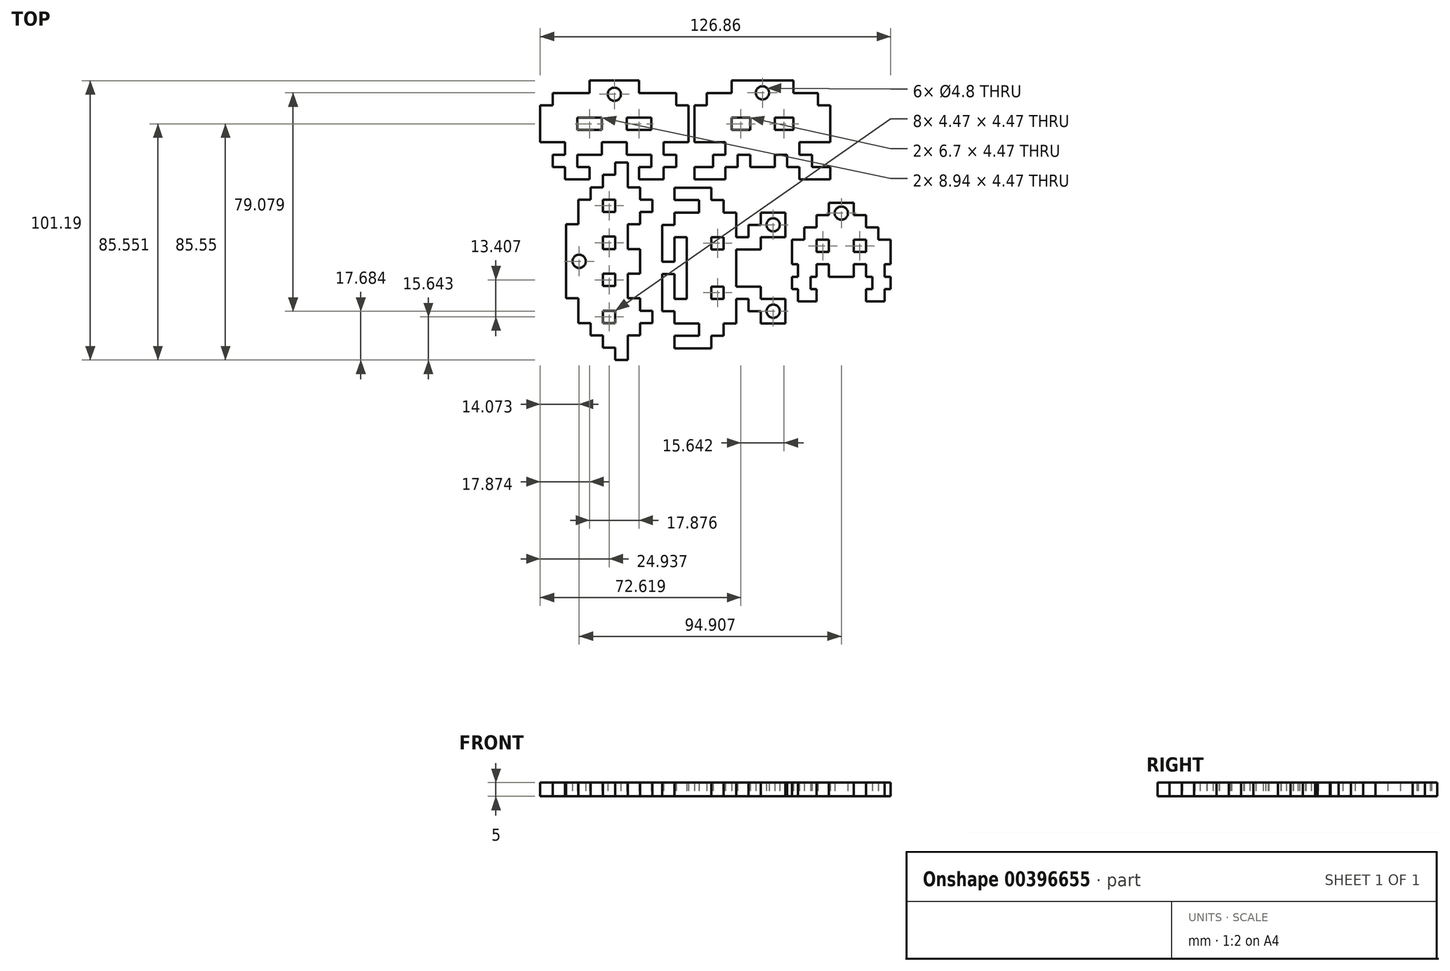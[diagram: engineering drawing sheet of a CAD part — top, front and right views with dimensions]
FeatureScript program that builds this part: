
annotation { "Feature Type Name" : "Feature", "Feature Type Description" : "" }
export const myFeature = defineFeature(function(context is Context, id is Id, definition is map)
    precondition{}
    {
        {
            var Q0;
            Q0=qCreatedBy(makeId("Top.planeOp"),FACE);
            var sketch = newSketch(context, id + "F0", { "sketchPlane" : qUnion([Q0])});
            skLineSegment(sketch, "E0", {"start": v(-759.07, 566.66) * mm, "end": v(-759.07, 641.14) * mm});
            skLineSegment(sketch, "E1", {"start": v(-759.07, 641.14) * mm, "end": v(-833.55, 641.14) * mm});
            skLineSegment(sketch, "E2", {"start": v(-833.55, 641.14) * mm, "end": v(-833.55, 715.62) * mm});
            skLineSegment(sketch, "E3", {"start": v(-833.55, 715.62) * mm, "end": v(-759.07, 715.62) * mm});
            skLineSegment(sketch, "E4", {"start": v(-759.07, 715.62) * mm, "end": v(-759.07, 790.1) * mm});
            skLineSegment(sketch, "E5", {"start": v(-759.07, 790.1) * mm, "end": v(-908.04, 790.1) * mm});
            skLineSegment(sketch, "E6", {"start": v(-908.04, 790.1) * mm, "end": v(-908.04, 1013.56) * mm});
            skLineSegment(sketch, "E7", {"start": v(-908.04, 1013.56) * mm, "end": v(-833.55, 1013.56) * mm});
            skLineSegment(sketch, "E8", {"start": v(-833.55, 1013.56) * mm, "end": v(-833.55, 1088.04) * mm});
            skLineSegment(sketch, "E9", {"start": v(-833.55, 1088.04) * mm, "end": v(-610.1, 1088.04) * mm});
            skLineSegment(sketch, "E10", {"start": v(-610.1, 1088.04) * mm, "end": v(-610.1, 1162.53) * mm});
            skLineSegment(sketch, "E11", {"start": v(-610.1, 1162.53) * mm, "end": v(-312.17, 1162.53) * mm});
            skLineSegment(sketch, "E12", {"start": v(-312.17, 1162.53) * mm, "end": v(-312.17, 1088.04) * mm});
            skLineSegment(sketch, "E13", {"start": v(-312.17, 1088.04) * mm, "end": v(-88.72, 1088.04) * mm});
            skLineSegment(sketch, "E14", {"start": v(-88.72, 1088.04) * mm, "end": v(-88.72, 1013.56) * mm});
            skLineSegment(sketch, "E15", {"start": v(-88.72, 1013.56) * mm, "end": v(-14.24, 1013.56) * mm});
            skLineSegment(sketch, "E16", {"start": v(-14.24, 1013.56) * mm, "end": v(-14.24, 790.1) * mm});
            skLineSegment(sketch, "E17", {"start": v(-14.24, 790.1) * mm, "end": v(-163.2, 790.1) * mm});
            skLineSegment(sketch, "E18", {"start": v(-163.2, 790.1) * mm, "end": v(-163.2, 715.62) * mm});
            skLineSegment(sketch, "E19", {"start": v(-163.2, 715.62) * mm, "end": v(-88.72, 715.62) * mm});
            skLineSegment(sketch, "E20", {"start": v(-88.72, 715.62) * mm, "end": v(-88.72, 641.14) * mm});
            skLineSegment(sketch, "E21", {"start": v(-88.72, 641.14) * mm, "end": v(-163.2, 641.14) * mm});
            skLineSegment(sketch, "E22", {"start": v(-163.2, 641.14) * mm, "end": v(-163.2, 566.66) * mm});
            skLineSegment(sketch, "E23", {"start": v(-163.2, 566.66) * mm, "end": v(-312.17, 566.66) * mm});
            skLineSegment(sketch, "E24", {"start": v(-312.17, 566.66) * mm, "end": v(-312.17, 641.14) * mm});
            skLineSegment(sketch, "E25", {"start": v(-312.17, 641.14) * mm, "end": v(-237.69, 641.14) * mm});
            skLineSegment(sketch, "E26", {"start": v(-237.69, 641.14) * mm, "end": v(-237.69, 715.62) * mm});
            skLineSegment(sketch, "E27", {"start": v(-237.69, 715.62) * mm, "end": v(-386.65, 715.62) * mm});
            skLineSegment(sketch, "E28", {"start": v(-386.65, 715.62) * mm, "end": v(-386.65, 790.1) * mm});
            skLineSegment(sketch, "E29", {"start": v(-386.65, 790.1) * mm, "end": v(-535.62, 790.1) * mm});
            skLineSegment(sketch, "E30", {"start": v(-535.62, 790.1) * mm, "end": v(-535.62, 715.62) * mm});
            skLineSegment(sketch, "E31", {"start": v(-535.62, 715.62) * mm, "end": v(-684.59, 715.62) * mm});
            skLineSegment(sketch, "E32", {"start": v(-684.59, 715.62) * mm, "end": v(-684.59, 641.14) * mm});
            skLineSegment(sketch, "E33", {"start": v(-684.59, 641.14) * mm, "end": v(-610.1, 641.14) * mm});
            skLineSegment(sketch, "E34", {"start": v(-610.1, 641.14) * mm, "end": v(-610.1, 566.66) * mm});
            skLineSegment(sketch, "E35", {"start": v(-610.1, 566.66) * mm, "end": v(-759.07, 566.66) * mm});
            skLineSegment(sketch, "E36", {"start": v(-535.62, 939.07) * mm, "end": v(-684.59, 939.07) * mm});
            skLineSegment(sketch, "E37", {"start": v(-684.59, 939.07) * mm, "end": v(-684.59, 864.59) * mm});
            skLineSegment(sketch, "E38", {"start": v(-684.59, 864.59) * mm, "end": v(-535.62, 864.59) * mm});
            skLineSegment(sketch, "E39", {"start": v(-535.62, 864.59) * mm, "end": v(-535.62, 939.07) * mm});
            skLineSegment(sketch, "E40", {"start": v(-237.69, 939.07) * mm, "end": v(-386.65, 939.07) * mm});
            skLineSegment(sketch, "E41", {"start": v(-386.65, 939.07) * mm, "end": v(-386.65, 864.59) * mm});
            skLineSegment(sketch, "E42", {"start": v(-386.65, 864.59) * mm, "end": v(-237.69, 864.59) * mm});
            skLineSegment(sketch, "E43", {"start": v(-237.69, 864.59) * mm, "end": v(-237.69, 939.07) * mm});
            skLineSegment(sketch, "E44", {"start": v(395.43, 1162.54) * mm, "end": v(618.88, 1162.54) * mm});
            skLineSegment(sketch, "E45", {"start": v(618.88, 1162.54) * mm, "end": v(618.88, 1088.05) * mm});
            skLineSegment(sketch, "E46", {"start": v(618.88, 1088.05) * mm, "end": v(767.84, 1088.05) * mm});
            skLineSegment(sketch, "E47", {"start": v(767.84, 1088.05) * mm, "end": v(767.84, 1013.57) * mm});
            skLineSegment(sketch, "E48", {"start": v(767.84, 1013.57) * mm, "end": v(842.33, 1013.57) * mm});
            skLineSegment(sketch, "E49", {"start": v(842.33, 1013.57) * mm, "end": v(842.33, 790.12) * mm});
            skLineSegment(sketch, "E50", {"start": v(842.33, 790.12) * mm, "end": v(656.13, 790.12) * mm});
            skLineSegment(sketch, "E51", {"start": v(656.13, 790.12) * mm, "end": v(656.13, 715.64) * mm});
            skLineSegment(sketch, "E52", {"start": v(656.13, 715.64) * mm, "end": v(730.6, 715.64) * mm});
            skLineSegment(sketch, "E53", {"start": v(730.6, 715.64) * mm, "end": v(730.6, 641.15) * mm});
            skLineSegment(sketch, "E54", {"start": v(730.6, 641.15) * mm, "end": v(767.84, 641.15) * mm});
            skLineSegment(sketch, "E55", {"start": v(767.84, 641.15) * mm, "end": v(842.33, 641.15) * mm});
            skLineSegment(sketch, "E56", {"start": v(842.33, 641.15) * mm, "end": v(842.33, 566.66) * mm});
            skLineSegment(sketch, "E57", {"start": v(842.33, 566.66) * mm, "end": v(656.12, 566.66) * mm});
            skLineSegment(sketch, "E58", {"start": v(656.12, 566.66) * mm, "end": v(656.12, 641.15) * mm});
            skLineSegment(sketch, "E59", {"start": v(656.12, 641.15) * mm, "end": v(581.64, 641.15) * mm});
            skLineSegment(sketch, "E60", {"start": v(581.64, 641.15) * mm, "end": v(581.64, 715.64) * mm});
            skLineSegment(sketch, "E61", {"start": v(581.64, 715.64) * mm, "end": v(507.15, 715.64) * mm});
            skLineSegment(sketch, "E62", {"start": v(507.15, 715.64) * mm, "end": v(507.16, 641.15) * mm});
            skLineSegment(sketch, "E63", {"start": v(507.16, 641.15) * mm, "end": v(358.18, 641.15) * mm});
            skLineSegment(sketch, "E64", {"start": v(358.18, 641.15) * mm, "end": v(358.18, 715.64) * mm});
            skLineSegment(sketch, "E65", {"start": v(358.18, 715.64) * mm, "end": v(283.7, 715.64) * mm});
            skLineSegment(sketch, "E66", {"start": v(283.7, 715.64) * mm, "end": v(283.7, 641.15) * mm});
            skLineSegment(sketch, "E67", {"start": v(283.7, 641.15) * mm, "end": v(209.22, 641.15) * mm});
            skLineSegment(sketch, "E68", {"start": v(209.22, 641.15) * mm, "end": v(209.22, 566.66) * mm});
            skLineSegment(sketch, "E69", {"start": v(209.22, 566.66) * mm, "end": v(23, 566.66) * mm});
            skLineSegment(sketch, "E70", {"start": v(23, 566.66) * mm, "end": v(23, 641.15) * mm});
            skLineSegment(sketch, "E71", {"start": v(23, 641.15) * mm, "end": v(134.73, 641.15) * mm});
            skLineSegment(sketch, "E72", {"start": v(134.73, 641.15) * mm, "end": v(134.73, 715.64) * mm});
            skLineSegment(sketch, "E73", {"start": v(134.73, 715.64) * mm, "end": v(209.22, 715.64) * mm});
            skLineSegment(sketch, "E74", {"start": v(209.22, 715.64) * mm, "end": v(209.22, 790.12) * mm});
            skLineSegment(sketch, "E75", {"start": v(209.22, 790.12) * mm, "end": v(23, 790.12) * mm});
            skLineSegment(sketch, "E76", {"start": v(23, 790.12) * mm, "end": v(23, 1013.57) * mm});
            skLineSegment(sketch, "E77", {"start": v(23, 1013.57) * mm, "end": v(97.5, 1013.57) * mm});
            skLineSegment(sketch, "E78", {"start": v(97.5, 1013.57) * mm, "end": v(97.5, 1088.05) * mm});
            skLineSegment(sketch, "E79", {"start": v(97.5, 1088.05) * mm, "end": v(246.46, 1088.05) * mm});
            skLineSegment(sketch, "E80", {"start": v(246.46, 1088.05) * mm, "end": v(246.46, 1162.54) * mm});
            skLineSegment(sketch, "E81", {"start": v(246.46, 1162.54) * mm, "end": v(395.43, 1162.54) * mm});
            skLineSegment(sketch, "E82", {"start": v(246.46, 864.6) * mm, "end": v(358.18, 864.6) * mm});
            skLineSegment(sketch, "E83", {"start": v(358.18, 864.6) * mm, "end": v(358.18, 939.09) * mm});
            skLineSegment(sketch, "E84", {"start": v(358.18, 939.09) * mm, "end": v(246.46, 939.09) * mm});
            skLineSegment(sketch, "E85", {"start": v(246.46, 939.09) * mm, "end": v(246.46, 864.6) * mm});
            skLineSegment(sketch, "E86", {"start": v(507.15, 864.6) * mm, "end": v(618.88, 864.6) * mm});
            skLineSegment(sketch, "E87", {"start": v(618.88, 864.6) * mm, "end": v(618.88, 939.09) * mm});
            skLineSegment(sketch, "E88", {"start": v(618.88, 939.09) * mm, "end": v(507.15, 939.09) * mm});
            skLineSegment(sketch, "E89", {"start": v(507.15, 939.09) * mm, "end": v(507.15, 864.6) * mm});
            skLineSegment(sketch, "E90", {"start": v(833.85, 425.85) * mm, "end": v(982.82, 425.85) * mm});
            skLineSegment(sketch, "E91", {"start": v(982.82, 425.85) * mm, "end": v(982.82, 351.36) * mm});
            skLineSegment(sketch, "E92", {"start": v(982.82, 351.36) * mm, "end": v(1057.3, 351.36) * mm});
            skLineSegment(sketch, "E93", {"start": v(1057.3, 351.36) * mm, "end": v(1057.3, 276.88) * mm});
            skLineSegment(sketch, "E94", {"start": v(1057.3, 276.88) * mm, "end": v(1131.78, 276.88) * mm});
            skLineSegment(sketch, "E95", {"start": v(1131.78, 276.88) * mm, "end": v(1131.78, 202.4) * mm});
            skLineSegment(sketch, "E96", {"start": v(1131.78, 202.4) * mm, "end": v(1206.27, 202.4) * mm});
            skLineSegment(sketch, "E97", {"start": v(1206.27, 202.4) * mm, "end": v(1206.27, 53.43) * mm});
            skLineSegment(sketch, "E98", {"start": v(1206.27, 53.43) * mm, "end": v(1169.03, 53.43) * mm});
            skLineSegment(sketch, "E99", {"start": v(1169.03, 53.43) * mm, "end": v(1169.03, -21.05) * mm});
            skLineSegment(sketch, "E100", {"start": v(1169.03, -21.05) * mm, "end": v(1206.27, -21.05) * mm});
            skLineSegment(sketch, "E101", {"start": v(1206.27, -21.05) * mm, "end": v(1206.27, -95.54) * mm});
            skLineSegment(sketch, "E102", {"start": v(1206.27, -95.54) * mm, "end": v(1169.03, -95.54) * mm});
            skLineSegment(sketch, "E103", {"start": v(1169.03, -95.54) * mm, "end": v(1169.03, -170.02) * mm});
            skLineSegment(sketch, "E104", {"start": v(1169.03, -170.02) * mm, "end": v(1057.3, -170.02) * mm});
            skLineSegment(sketch, "E105", {"start": v(1057.3, -170.02) * mm, "end": v(1057.3, -95.54) * mm});
            skLineSegment(sketch, "E106", {"start": v(1057.3, -95.54) * mm, "end": v(1094.54, -95.54) * mm});
            skLineSegment(sketch, "E107", {"start": v(1094.54, -95.54) * mm, "end": v(1094.54, -21.05) * mm});
            skLineSegment(sketch, "E108", {"start": v(1094.54, -21.05) * mm, "end": v(1057.3, -21.05) * mm});
            skLineSegment(sketch, "E109", {"start": v(1057.3, -21.05) * mm, "end": v(1057.3, 53.43) * mm});
            skLineSegment(sketch, "E110", {"start": v(1057.3, 53.43) * mm, "end": v(982.82, 53.43) * mm});
            skLineSegment(sketch, "E111", {"start": v(982.82, 53.43) * mm, "end": v(982.82, -21.05) * mm});
            skLineSegment(sketch, "E112", {"start": v(982.82, -21.05) * mm, "end": v(833.85, -21.05) * mm});
            skLineSegment(sketch, "E113", {"start": v(833.85, -21.05) * mm, "end": v(833.85, 53.43) * mm});
            skLineSegment(sketch, "E114", {"start": v(833.85, 53.43) * mm, "end": v(759.37, 53.43) * mm});
            skLineSegment(sketch, "E115", {"start": v(759.37, 53.43) * mm, "end": v(759.37, -21.05) * mm});
            skLineSegment(sketch, "E116", {"start": v(759.37, -21.05) * mm, "end": v(722.13, -21.05) * mm});
            skLineSegment(sketch, "E117", {"start": v(722.13, -21.05) * mm, "end": v(722.13, -95.54) * mm});
            skLineSegment(sketch, "E118", {"start": v(722.13, -95.54) * mm, "end": v(759.37, -95.54) * mm});
            skLineSegment(sketch, "E119", {"start": v(759.37, -95.54) * mm, "end": v(759.37, -170.02) * mm});
            skLineSegment(sketch, "E120", {"start": v(759.37, -170.02) * mm, "end": v(647.64, -170.02) * mm});
            skLineSegment(sketch, "E121", {"start": v(647.64, -170.02) * mm, "end": v(647.64, -95.54) * mm});
            skLineSegment(sketch, "E122", {"start": v(647.64, -95.54) * mm, "end": v(610.4, -95.54) * mm});
            skLineSegment(sketch, "E123", {"start": v(610.4, -95.54) * mm, "end": v(610.4, -21.05) * mm});
            skLineSegment(sketch, "E124", {"start": v(610.4, -21.05) * mm, "end": v(647.64, -21.05) * mm});
            skLineSegment(sketch, "E125", {"start": v(647.64, -21.05) * mm, "end": v(647.64, 53.43) * mm});
            skLineSegment(sketch, "E126", {"start": v(647.64, 53.43) * mm, "end": v(610.4, 53.43) * mm});
            skLineSegment(sketch, "E127", {"start": v(610.4, 53.43) * mm, "end": v(610.4, 202.4) * mm});
            skLineSegment(sketch, "E128", {"start": v(610.4, 202.4) * mm, "end": v(684.88, 202.4) * mm});
            skLineSegment(sketch, "E129", {"start": v(684.88, 202.4) * mm, "end": v(684.88, 276.88) * mm});
            skLineSegment(sketch, "E130", {"start": v(684.88, 276.88) * mm, "end": v(759.37, 276.88) * mm});
            skLineSegment(sketch, "E131", {"start": v(759.37, 276.88) * mm, "end": v(759.37, 351.36) * mm});
            skLineSegment(sketch, "E132", {"start": v(759.37, 351.36) * mm, "end": v(833.85, 351.36) * mm});
            skLineSegment(sketch, "E133", {"start": v(833.85, 351.36) * mm, "end": v(833.85, 425.85) * mm});
            skLineSegment(sketch, "E134", {"start": v(833.85, 127.91) * mm, "end": v(759.37, 127.91) * mm});
            skLineSegment(sketch, "E135", {"start": v(759.37, 127.91) * mm, "end": v(759.37, 202.4) * mm});
            skLineSegment(sketch, "E136", {"start": v(759.37, 202.4) * mm, "end": v(833.85, 202.4) * mm});
            skLineSegment(sketch, "E137", {"start": v(833.85, 202.4) * mm, "end": v(833.85, 127.91) * mm});
            skLineSegment(sketch, "E138", {"start": v(982.82, 127.91) * mm, "end": v(1057.3, 127.91) * mm});
            skLineSegment(sketch, "E139", {"start": v(1057.3, 127.91) * mm, "end": v(1057.3, 202.4) * mm});
            skLineSegment(sketch, "E140", {"start": v(1057.3, 202.4) * mm, "end": v(982.82, 202.4) * mm});
            skLineSegment(sketch, "E141", {"start": v(982.82, 202.4) * mm, "end": v(982.82, 127.91) * mm});
            skLineSegment(sketch, "E142", {"start": v(2475.62, -2472.72) * mm, "end": v(2438.37, -2435.47) * mm});
            skLineSegment(sketch, "E143", {"start": v(-173.18, 68.67) * mm, "end": v(-98.7, 68.67) * mm});
            skLineSegment(sketch, "E144", {"start": v(-98.7, 68.67) * mm, "end": v(-98.7, 217.64) * mm});
            skLineSegment(sketch, "E145", {"start": v(-98.7, 217.64) * mm, "end": v(-24.22, 217.64) * mm});
            skLineSegment(sketch, "E146", {"start": v(-24.22, 217.64) * mm, "end": v(-24.22, -154.78) * mm});
            skLineSegment(sketch, "E147", {"start": v(-24.22, -154.78) * mm, "end": v(-98.7, -154.78) * mm});
            skLineSegment(sketch, "E148", {"start": v(-98.7, -154.78) * mm, "end": v(-98.7, -5.81) * mm});
            skLineSegment(sketch, "E149", {"start": v(-98.7, -5.81) * mm, "end": v(-173.18, -5.81) * mm});
            skLineSegment(sketch, "E150", {"start": v(-173.18, -5.81) * mm, "end": v(-173.18, -117.54) * mm});
            skLineSegment(sketch, "E151", {"start": v(-173.18, -117.54) * mm, "end": v(-173.18, -229.26) * mm});
            skLineSegment(sketch, "E152", {"start": v(-173.18, -229.26) * mm, "end": v(-98.7, -229.26) * mm});
            skLineSegment(sketch, "E153", {"start": v(-98.7, -229.26) * mm, "end": v(-98.7, -303.75) * mm});
            skLineSegment(sketch, "E154", {"start": v(-98.7, -303.75) * mm, "end": v(50.27, -303.75) * mm});
            skLineSegment(sketch, "E155", {"start": v(50.27, -303.75) * mm, "end": v(50.27, -378.23) * mm});
            skLineSegment(sketch, "E156", {"start": v(50.27, -378.23) * mm, "end": v(-98.7, -378.23) * mm});
            skLineSegment(sketch, "E157", {"start": v(-98.7, -378.23) * mm, "end": v(-98.7, -452.71) * mm});
            skLineSegment(sketch, "E158", {"start": v(-98.7, -452.71) * mm, "end": v(124.75, -452.71) * mm});
            skLineSegment(sketch, "E159", {"start": v(124.75, -452.71) * mm, "end": v(124.75, -378.23) * mm});
            skLineSegment(sketch, "E160", {"start": v(124.75, -378.23) * mm, "end": v(199.23, -378.23) * mm});
            skLineSegment(sketch, "E161", {"start": v(199.23, -378.23) * mm, "end": v(199.23, -303.75) * mm});
            skLineSegment(sketch, "E162", {"start": v(199.23, -303.75) * mm, "end": v(273.72, -303.75) * mm});
            skLineSegment(sketch, "E163", {"start": v(273.72, -303.75) * mm, "end": v(273.72, -229.26) * mm});
            skLineSegment(sketch, "E164", {"start": v(273.72, -229.26) * mm, "end": v(273.72, -154.78) * mm});
            skLineSegment(sketch, "E165", {"start": v(273.72, -154.78) * mm, "end": v(348.2, -154.78) * mm});
            skLineSegment(sketch, "E166", {"start": v(348.2, -154.78) * mm, "end": v(348.2, -229.26) * mm});
            skLineSegment(sketch, "E167", {"start": v(348.2, -229.26) * mm, "end": v(422.68, -229.26) * mm});
            skLineSegment(sketch, "E168", {"start": v(422.68, -229.26) * mm, "end": v(422.68, -303.75) * mm});
            skLineSegment(sketch, "E169", {"start": v(422.68, -303.75) * mm, "end": v(571.65, -303.75) * mm});
            skLineSegment(sketch, "E170", {"start": v(571.65, -303.75) * mm, "end": v(571.65, -154.78) * mm});
            skLineSegment(sketch, "E171", {"start": v(571.65, -154.78) * mm, "end": v(422.68, -154.78) * mm});
            skLineSegment(sketch, "E172", {"start": v(422.68, -154.78) * mm, "end": v(422.3, -88.2) * mm});
            skLineSegment(sketch, "E173", {"start": v(422.3, -88.2) * mm, "end": v(422.68, -80.3) * mm});
            skLineSegment(sketch, "E174", {"start": v(422.68, -80.3) * mm, "end": v(273.72, -80.3) * mm});
            skLineSegment(sketch, "E175", {"start": v(273.72, -80.3) * mm, "end": v(273.72, 143.15) * mm});
            skLineSegment(sketch, "E176", {"start": v(273.72, 143.15) * mm, "end": v(422.68, 143.15) * mm});
            skLineSegment(sketch, "E177", {"start": v(422.68, 143.15) * mm, "end": v(422.68, 217.64) * mm});
            skLineSegment(sketch, "E178", {"start": v(422.68, 217.64) * mm, "end": v(571.65, 217.64) * mm});
            skLineSegment(sketch, "E179", {"start": v(571.65, 217.64) * mm, "end": v(571.65, 366.6) * mm});
            skLineSegment(sketch, "E180", {"start": v(571.65, 366.6) * mm, "end": v(422.68, 366.6) * mm});
            skLineSegment(sketch, "E181", {"start": v(422.68, 366.6) * mm, "end": v(422.68, 292.12) * mm});
            skLineSegment(sketch, "E182", {"start": v(422.68, 292.12) * mm, "end": v(348.2, 292.12) * mm});
            skLineSegment(sketch, "E183", {"start": v(348.2, 292.12) * mm, "end": v(348.2, 217.64) * mm});
            skLineSegment(sketch, "E184", {"start": v(348.2, 217.64) * mm, "end": v(273.72, 217.64) * mm});
            skLineSegment(sketch, "E185", {"start": v(273.72, 217.64) * mm, "end": v(273.72, 366.6) * mm});
            skLineSegment(sketch, "E186", {"start": v(273.72, 366.6) * mm, "end": v(199.23, 366.6) * mm});
            skLineSegment(sketch, "E187", {"start": v(199.23, 366.6) * mm, "end": v(199.23, 441.09) * mm});
            skLineSegment(sketch, "E188", {"start": v(199.23, 441.09) * mm, "end": v(124.75, 441.09) * mm});
            skLineSegment(sketch, "E189", {"start": v(124.75, 441.09) * mm, "end": v(124.75, 515.57) * mm});
            skLineSegment(sketch, "E190", {"start": v(124.75, 515.57) * mm, "end": v(-98.7, 515.57) * mm});
            skLineSegment(sketch, "E191", {"start": v(-98.7, 515.57) * mm, "end": v(-98.7, 441.09) * mm});
            skLineSegment(sketch, "E192", {"start": v(-98.7, 441.09) * mm, "end": v(50.27, 441.09) * mm});
            skLineSegment(sketch, "E193", {"start": v(50.27, 441.09) * mm, "end": v(50.27, 366.6) * mm});
            skLineSegment(sketch, "E194", {"start": v(50.27, 366.6) * mm, "end": v(-98.7, 366.6) * mm});
            skLineSegment(sketch, "E195", {"start": v(-98.7, 366.6) * mm, "end": v(-98.7, 292.12) * mm});
            skLineSegment(sketch, "E196", {"start": v(-98.7, 292.12) * mm, "end": v(-173.18, 292.12) * mm});
            skLineSegment(sketch, "E197", {"start": v(-173.18, 292.12) * mm, "end": v(-173.18, 68.67) * mm});
            skLineSegment(sketch, "E198", {"start": v(199.23, 217.64) * mm, "end": v(124.75, 217.64) * mm});
            skLineSegment(sketch, "E199", {"start": v(124.75, 217.64) * mm, "end": v(124.75, 143.15) * mm});
            skLineSegment(sketch, "E200", {"start": v(124.75, 143.15) * mm, "end": v(199.23, 143.15) * mm});
            skLineSegment(sketch, "E201", {"start": v(199.23, 143.15) * mm, "end": v(199.23, 217.64) * mm});
            skLineSegment(sketch, "E202", {"start": v(199.23, -80.3) * mm, "end": v(124.75, -80.3) * mm});
            skLineSegment(sketch, "E203", {"start": v(124.75, -80.3) * mm, "end": v(124.75, -154.78) * mm});
            skLineSegment(sketch, "E204", {"start": v(124.75, -154.78) * mm, "end": v(199.23, -154.78) * mm});
            skLineSegment(sketch, "E205", {"start": v(199.23, -154.78) * mm, "end": v(199.23, -80.3) * mm});
            skLineSegment(sketch, "E206", {"start": v(-678.6, -300.53) * mm, "end": v(-604.1, -300.53) * mm});
            skLineSegment(sketch, "E207", {"start": v(-604.1, -300.53) * mm, "end": v(-604.1, -375) * mm});
            skLineSegment(sketch, "E208", {"start": v(-604.1, -375) * mm, "end": v(-529.63, -375) * mm});
            skLineSegment(sketch, "E209", {"start": v(-529.63, -375) * mm, "end": v(-529.63, -449.5) * mm});
            skLineSegment(sketch, "E210", {"start": v(-529.63, -449.5) * mm, "end": v(-455.14, -449.5) * mm});
            skLineSegment(sketch, "E211", {"start": v(-455.14, -449.5) * mm, "end": v(-455.14, -523.98) * mm});
            skLineSegment(sketch, "E212", {"start": v(-455.14, -523.98) * mm, "end": v(-380.66, -523.98) * mm});
            skLineSegment(sketch, "E213", {"start": v(-380.66, -523.98) * mm, "end": v(-380.66, -375) * mm});
            skLineSegment(sketch, "E214", {"start": v(-380.66, -375) * mm, "end": v(-306.17, -375) * mm});
            skLineSegment(sketch, "E215", {"start": v(-306.17, -375) * mm, "end": v(-306.17, -300.53) * mm});
            skLineSegment(sketch, "E216", {"start": v(-306.17, -300.53) * mm, "end": v(-231.67, -300.53) * mm});
            skLineSegment(sketch, "E217", {"start": v(-231.67, -300.53) * mm, "end": v(-231.67, -226.04) * mm});
            skLineSegment(sketch, "E218", {"start": v(-231.67, -226.04) * mm, "end": v(-306.17, -226.04) * mm});
            skLineSegment(sketch, "E219", {"start": v(-306.17, -226.04) * mm, "end": v(-306.17, -151.56) * mm});
            skLineSegment(sketch, "E220", {"start": v(-306.17, -151.56) * mm, "end": v(-380.66, -151.56) * mm});
            skLineSegment(sketch, "E221", {"start": v(-380.66, -151.56) * mm, "end": v(-380.66, -2.6) * mm});
            skLineSegment(sketch, "E222", {"start": v(-380.66, -2.6) * mm, "end": v(-306.17, -2.6) * mm});
            skLineSegment(sketch, "E223", {"start": v(-306.17, -2.6) * mm, "end": v(-306.17, 146.38) * mm});
            skLineSegment(sketch, "E224", {"start": v(-306.17, 146.38) * mm, "end": v(-380.66, 146.38) * mm});
            skLineSegment(sketch, "E225", {"start": v(-380.66, 146.38) * mm, "end": v(-380.66, 295.34) * mm});
            skLineSegment(sketch, "E226", {"start": v(-380.66, 295.34) * mm, "end": v(-306.17, 295.34) * mm});
            skLineSegment(sketch, "E227", {"start": v(-306.17, 295.34) * mm, "end": v(-306.17, 369.83) * mm});
            skLineSegment(sketch, "E228", {"start": v(-306.17, 369.83) * mm, "end": v(-231.67, 369.83) * mm});
            skLineSegment(sketch, "E229", {"start": v(-231.67, 369.83) * mm, "end": v(-231.67, 444.3) * mm});
            skLineSegment(sketch, "E230", {"start": v(-231.67, 444.3) * mm, "end": v(-306.17, 444.3) * mm});
            skLineSegment(sketch, "E231", {"start": v(-306.17, 444.3) * mm, "end": v(-306.17, 518.8) * mm});
            skLineSegment(sketch, "E232", {"start": v(-306.17, 518.8) * mm, "end": v(-380.66, 518.8) * mm});
            skLineSegment(sketch, "E233", {"start": v(-380.66, 518.8) * mm, "end": v(-380.66, 667.76) * mm});
            skLineSegment(sketch, "E234", {"start": v(-380.66, 667.76) * mm, "end": v(-455.14, 667.76) * mm});
            skLineSegment(sketch, "E235", {"start": v(-455.14, 667.76) * mm, "end": v(-455.14, 593.28) * mm});
            skLineSegment(sketch, "E236", {"start": v(-455.14, 593.28) * mm, "end": v(-529.63, 593.28) * mm});
            skLineSegment(sketch, "E237", {"start": v(-529.63, 593.28) * mm, "end": v(-529.63, 518.8) * mm});
            skLineSegment(sketch, "E238", {"start": v(-529.63, 518.8) * mm, "end": v(-604.1, 518.8) * mm});
            skLineSegment(sketch, "E239", {"start": v(-604.1, 518.8) * mm, "end": v(-604.1, 444.3) * mm});
            skLineSegment(sketch, "E240", {"start": v(-604.1, 444.3) * mm, "end": v(-678.6, 444.3) * mm});
            skLineSegment(sketch, "E241", {"start": v(-678.6, 444.3) * mm, "end": v(-678.6, 295.34) * mm});
            skLineSegment(sketch, "E242", {"start": v(-678.6, 295.34) * mm, "end": v(-753.08, 295.34) * mm});
            skLineSegment(sketch, "E243", {"start": v(-753.08, 295.34) * mm, "end": v(-753.08, -151.56) * mm});
            skLineSegment(sketch, "E244", {"start": v(-753.08, -151.56) * mm, "end": v(-678.6, -151.56) * mm});
            skLineSegment(sketch, "E245", {"start": v(-678.6, -151.56) * mm, "end": v(-678.6, -300.53) * mm});
            skLineSegment(sketch, "E246", {"start": v(-529.63, -226.04) * mm, "end": v(-529.63, -300.53) * mm});
            skLineSegment(sketch, "E247", {"start": v(-529.63, -300.53) * mm, "end": v(-455.14, -300.53) * mm});
            skLineSegment(sketch, "E248", {"start": v(-455.14, -300.53) * mm, "end": v(-455.14, -226.04) * mm});
            skLineSegment(sketch, "E249", {"start": v(-455.14, -226.04) * mm, "end": v(-529.63, -226.04) * mm});
            skLineSegment(sketch, "E250", {"start": v(-529.63, 369.83) * mm, "end": v(-529.63, 444.3) * mm});
            skLineSegment(sketch, "E251", {"start": v(-529.63, 444.3) * mm, "end": v(-455.14, 444.3) * mm});
            skLineSegment(sketch, "E252", {"start": v(-455.14, 444.3) * mm, "end": v(-455.14, 369.83) * mm});
            skLineSegment(sketch, "E253", {"start": v(-455.14, 369.83) * mm, "end": v(-529.63, 369.83) * mm});
            skLineSegment(sketch, "E254", {"start": v(-529.63, 146.38) * mm, "end": v(-529.63, 220.86) * mm});
            skLineSegment(sketch, "E255", {"start": v(-529.63, 220.86) * mm, "end": v(-455.14, 220.86) * mm});
            skLineSegment(sketch, "E256", {"start": v(-455.14, 220.86) * mm, "end": v(-455.14, 146.38) * mm});
            skLineSegment(sketch, "E257", {"start": v(-455.14, 146.38) * mm, "end": v(-529.63, 146.38) * mm});
            skLineSegment(sketch, "E258", {"start": v(-529.63, -77.08) * mm, "end": v(-529.63, -2.6) * mm});
            skLineSegment(sketch, "E259", {"start": v(-529.63, -2.6) * mm, "end": v(-455.14, -2.6) * mm});
            skLineSegment(sketch, "E260", {"start": v(-455.14, -2.6) * mm, "end": v(-455.14, -77.08) * mm});
            skLineSegment(sketch, "E261", {"start": v(-455.14, -77.08) * mm, "end": v(-529.63, -77.08) * mm});
            skCircle(sketch, "E262", {"center": v(497.17, 292.12) * mm, "radius": 40 * mm});
            skPoint(sketch, "E262.centerSnap0", {"position": v(497.17, 366.6) * mm});
            skPoint(sketch, "E262.centerSnap1", {"position": v(571.65, 292.12) * mm});
            skCircle(sketch, "E263", {"center": v(497.17, -229.26) * mm, "radius": 40 * mm});
            skPoint(sketch, "E263.centerSnap0", {"position": v(571.65, -229.26) * mm});
            skPoint(sketch, "E263.centerSnap1", {"position": v(497.17, -154.78) * mm});
            skCircle(sketch, "E264", {"center": v(908.33, 362.63) * mm, "radius": 40 * mm});
            skPoint(sketch, "E264.centerSnap0", {"position": v(908.33, 425.85) * mm});
            skCircle(sketch, "E265", {"center": v(-673.46, 71.9) * mm, "radius": 40 * mm});
            skPoint(sketch, "E265.centerSnap0", {"position": v(-753.08, 71.9) * mm});
            skCircle(sketch, "E266", {"center": v(-461.14, 1080.22) * mm, "radius": 40 * mm});
            skPoint(sketch, "E266.centerSnap0", {"position": v(-461.14, 1162.53) * mm});
            skCircle(sketch, "E267", {"center": v(432.67, 1088.72) * mm, "radius": 40 * mm});
            skPoint(sketch, "E267.centerSnap0", {"position": v(432.67, 641.15) * mm});
            skSolve(sketch);
        }
        {
            var Q0;
            Q0=makeQuery(id+"F0.imprint","IMPRINT",FACE,{"disambiguationData":[TD([[makeQuery(id+"F0.imprint","IMPRINT",EDGE,{"derivedFrom":sQuery(id+"F0.wireOp",EDGE,"E0")}),-1.0]])]});
            var Q1;
            Q1=makeQuery(id+"F0.imprint","IMPRINT",FACE,{"disambiguationData":[TD([[makeQuery(id+"F0.imprint","IMPRINT",EDGE,{"derivedFrom":sQuery(id+"F0.wireOp",EDGE,"E206")}),1.0]])]});
            var Q2;
            Q2=makeQuery(id+"F0.imprint","IMPRINT",FACE,{"disambiguationData":[TD([[makeQuery(id+"F0.imprint","IMPRINT",EDGE,{"derivedFrom":sQuery(id+"F0.wireOp",EDGE,"E143")}),1.0]])]});
            var Q3;
            Q3=makeQuery(id+"F0.imprint","IMPRINT",FACE,{"disambiguationData":[TD([[makeQuery(id+"F0.imprint","IMPRINT",EDGE,{"derivedFrom":sQuery(id+"F0.wireOp",EDGE,"E44")}),-1.0]])]});
            var Q4;
            Q4=makeQuery(id+"F0.imprint","IMPRINT",FACE,{"disambiguationData":[TD([[makeQuery(id+"F0.imprint","IMPRINT",EDGE,{"derivedFrom":sQuery(id+"F0.wireOp",EDGE,"E90")}),-1.0]])]});
            var Q5;
            Q5=sQuery(id+"F0.wireOp",EDGE,"E46");
            var Q6;
            Q6=sQuery(id+"F0.wireOp",EDGE,"E190");
            var Q7;
            Q7=sQuery(id+"F0.wireOp",EDGE,"E158");
            var Q8;
            Q8=sQuery(id+"F0.wireOp",EDGE,"E174");
            var Q9;
            Q9=sQuery(id+"F0.wireOp",EDGE,"E221");
            var Q10;
            Q10=sQuery(id+"F0.wireOp",EDGE,"E29");
            var Q11;
            Q11=sQuery(id+"F0.wireOp",EDGE,"E175");
            var Q12;
            Q12=sQuery(id+"F0.wireOp",EDGE,"E223");
            var Q13;
            Q13=sQuery(id+"F0.wireOp",EDGE,"E79");
            var Q14;
            Q14=sQuery(id+"F0.wireOp",EDGE,"E63");
            var Q15;
            Q15=sQuery(id+"F0.wireOp",EDGE,"E31");
            var Q16;
            Q16=sQuery(id+"F0.wireOp",EDGE,"E127");
            var Q17;
            Q17=sQuery(id+"F0.wireOp",EDGE,"E176");
            var Q18;
            Q18=sQuery(id+"F0.wireOp",EDGE,"E192");
            var Q19;
            Q19=sQuery(id+"F0.wireOp",EDGE,"E16");
            var Q20;
            Q20=sQuery(id+"F0.wireOp",EDGE,"E144");
            var Q21;
            Q21=sQuery(id+"F0.wireOp",EDGE,"E112");
            var Q22;
            Q22=sQuery(id+"F0.wireOp",EDGE,"E23");
            var Q23;
            Q23=sQuery(id+"F0.wireOp",EDGE,"E49");
            var Q24;
            Q24=sQuery(id+"F0.wireOp",EDGE,"E17");
            var Q25;
            Q25=sQuery(id+"F0.wireOp",EDGE,"E97");
            var Q26;
            Q26=sQuery(id+"F0.wireOp",EDGE,"E81");
            var Q27;
            Q27=sQuery(id+"F0.wireOp",EDGE,"E241");
            var Q28;
            Q28=sQuery(id+"F0.wireOp",EDGE,"E225");
            var Q29;
            Q29=sQuery(id+"F0.wireOp",EDGE,"E40");
            var Q30;
            Q30=sQuery(id+"F0.wireOp",EDGE,"E50");
            var Q31;
            Q31=sQuery(id+"F0.wireOp",EDGE,"E146");
            var Q32;
            Q32=sQuery(id+"F0.wireOp",EDGE,"E194");
            var Q33;
            Q33=sQuery(id+"F0.wireOp",EDGE,"E178");
            var Q34;
            Q34=sQuery(id+"F0.wireOp",EDGE,"E57");
            var Q35;
            Q35=sQuery(id+"F0.wireOp",EDGE,"E185");
            var Q36;
            Q36=sQuery(id+"F0.wireOp",EDGE,"E169");
            var Q37;
            Q37=sQuery(id+"F0.wireOp",EDGE,"E35");
            var Q38;
            Q38=sQuery(id+"F0.wireOp",EDGE,"E179");
            var Q39;
            Q39=sQuery(id+"F0.wireOp",EDGE,"E243");
            var Q40;
            Q40=sQuery(id+"F0.wireOp",EDGE,"E42");
            var Q41;
            Q41=sQuery(id+"F0.wireOp",EDGE,"E90");
            var Q42;
            Q42=sQuery(id+"F0.wireOp",EDGE,"E170");
            var Q43;
            Q43=sQuery(id+"F0.wireOp",EDGE,"E154");
            var Q44;
            Q44=sQuery(id+"F0.wireOp",EDGE,"E36");
            var Q45;
            Q45=sQuery(id+"F0.wireOp",EDGE,"E148");
            var Q46;
            Q46=sQuery(id+"F0.wireOp",EDGE,"E180");
            var Q47;
            Q47=sQuery(id+"F0.wireOp",EDGE,"E27");
            var Q48;
            Q48=sQuery(id+"F0.wireOp",EDGE,"E75");
            var Q49;
            Q49=sQuery(id+"F0.wireOp",EDGE,"E171");
            var Q50;
            Q50=sQuery(id+"F0.wireOp",EDGE,"E213");
            var Q51;
            Q51=sQuery(id+"F0.wireOp",EDGE,"E197");
            var Q52;
            Q52=sQuery(id+"F0.wireOp",EDGE,"E245");
            var Q53;
            Q53=sQuery(id+"F0.wireOp",EDGE,"E44");
            var Q54;
            Q54=sQuery(id+"F0.wireOp",EDGE,"E76");
            var Q55;
            Q55=sQuery(id+"F0.wireOp",EDGE,"E156");
            var Q56;
            Q56=sQuery(id+"F0.wireOp",EDGE,"E38");
            var Q57;
            Q57=sQuery(id+"F0.wireOp",EDGE,"E13");
            var Q58;
            Q58=sQuery(id+"F0.wireOp",EDGE,"E5");
            var Q59;
            Q59=sQuery(id+"F0.wireOp",EDGE,"E6");
            var Q60;
            Q60=sQuery(id+"F0.wireOp",EDGE,"E9");
            var Q61;
            Q61=sQuery(id+"F0.wireOp",EDGE,"E11");
            var Q62;
            Q62=sQuery(id+"F0.wireOp",EDGE,"E44");
            var Q63;
            Q63=sQuery(id+"F0.wireOp",EDGE,"E76");
            var Q64;
            Q64=sQuery(id+"F0.wireOp",EDGE,"E97");
            var Q65;
            Q65=sQuery(id+"F0.wireOp",EDGE,"E49");
            var Q66;
            Q66=sQuery(id+"F0.wireOp",EDGE,"E81");
            var Q67;
            Q67=sQuery(id+"F0.wireOp",EDGE,"E17");
            var Q68;
            Q68=sQuery(id+"F0.wireOp",EDGE,"E171");
            var Q69;
            Q69=sQuery(id+"F0.wireOp",EDGE,"E27");
            var Q70;
            Q70=sQuery(id+"F0.wireOp",EDGE,"E75");
            var Q71;
            Q71=sQuery(id+"F0.wireOp",EDGE,"E225");
            var Q72;
            Q72=sQuery(id+"F0.wireOp",EDGE,"E241");
            var Q73;
            Q73=sQuery(id+"F0.wireOp",EDGE,"E11");
            var Q74;
            Q74=sQuery(id+"F0.wireOp",EDGE,"E16");
            var Q75;
            Q75=sQuery(id+"F0.wireOp",EDGE,"E154");
            var Q76;
            Q76=sQuery(id+"F0.wireOp",EDGE,"E170");
            var Q77;
            Q77=sQuery(id+"F0.wireOp",EDGE,"E90");
            var Q78;
            Q78=sQuery(id+"F0.wireOp",EDGE,"E42");
            var Q79;
            Q79=sQuery(id+"F0.wireOp",EDGE,"E176");
            var Q80;
            Q80=sQuery(id+"F0.wireOp",EDGE,"E192");
            var Q81;
            Q81=sQuery(id+"F0.wireOp",EDGE,"E112");
            var Q82;
            Q82=sQuery(id+"F0.wireOp",EDGE,"E144");
            var Q83;
            Q83=sQuery(id+"F0.wireOp",EDGE,"E57");
            var Q84;
            Q84=sQuery(id+"F0.wireOp",EDGE,"E223");
            var Q85;
            Q85=sQuery(id+"F0.wireOp",EDGE,"E9");
            var Q86;
            Q86=sQuery(id+"F0.wireOp",EDGE,"E175");
            var Q87;
            Q87=sQuery(id+"F0.wireOp",EDGE,"E127");
            var Q88;
            Q88=sQuery(id+"F0.wireOp",EDGE,"E31");
            var Q89;
            Q89=sQuery(id+"F0.wireOp",EDGE,"E63");
            var Q90;
            Q90=sQuery(id+"F0.wireOp",EDGE,"E79");
            var Q91;
            Q91=sQuery(id+"F0.wireOp",EDGE,"E185");
            var Q92;
            Q92=sQuery(id+"F0.wireOp",EDGE,"E169");
            var Q93;
            Q93=sQuery(id+"F0.wireOp",EDGE,"E40");
            var Q94;
            Q94=sQuery(id+"F0.wireOp",EDGE,"E158");
            var Q95;
            Q95=sQuery(id+"F0.wireOp",EDGE,"E174");
            var Q96;
            Q96=sQuery(id+"F0.wireOp",EDGE,"E190");
            var Q97;
            Q97=sQuery(id+"F0.wireOp",EDGE,"E46");
            var Q98;
            Q98=sQuery(id+"F0.wireOp",EDGE,"E23");
            var Q99;
            Q99=sQuery(id+"F0.wireOp",EDGE,"E221");
            var Q100;
            Q100=sQuery(id+"F0.wireOp",EDGE,"E180");
            var Q101;
            Q101=sQuery(id+"F0.wireOp",EDGE,"E148");
            var Q102;
            Q102=sQuery(id+"F0.wireOp",EDGE,"E36");
            var Q103;
            Q103=sQuery(id+"F0.wireOp",EDGE,"E29");
            var Q104;
            Q104=sQuery(id+"F0.wireOp",EDGE,"E243");
            var Q105;
            Q105=sQuery(id+"F0.wireOp",EDGE,"E13");
            var Q106;
            Q106=sQuery(id+"F0.wireOp",EDGE,"E179");
            var Q107;
            Q107=sQuery(id+"F0.wireOp",EDGE,"E35");
            var Q108;
            Q108=sQuery(id+"F0.wireOp",EDGE,"E178");
            var Q109;
            Q109=sQuery(id+"F0.wireOp",EDGE,"E194");
            var Q110;
            Q110=sQuery(id+"F0.wireOp",EDGE,"E146");
            var Q111;
            Q111=sQuery(id+"F0.wireOp",EDGE,"E50");
            var Q112;
            Q112=sQuery(id+"F0.wireOp",EDGE,"E156");
            var Q113;
            Q113=sQuery(id+"F0.wireOp",EDGE,"E213");
            var Q114;
            Q114=sQuery(id+"F0.wireOp",EDGE,"E197");
            var Q115;
            Q115=sQuery(id+"F0.wireOp",EDGE,"E245");
            var Q116;
            Q116=sQuery(id+"F0.wireOp",EDGE,"E38");
            var Q117;
            Q117=sQuery(id+"F0.wireOp",EDGE,"E5");
            var Q118;
            Q118=sQuery(id+"F0.wireOp",EDGE,"E6");
            var Q119;
            Q119=sQuery(id+"F0.wireOp",EDGE,"E30");
            var Q120;
            Q120=sQuery(id+"F0.wireOp",EDGE,"E62");
            var Q121;
            Q121=sQuery(id+"F0.wireOp",EDGE,"E78");
            var Q122;
            Q122=sQuery(id+"F0.wireOp",EDGE,"E254");
            var Q123;
            Q123=sQuery(id+"F0.wireOp",EDGE,"E222");
            var Q124;
            Q124=sQuery(id+"F0.wireOp",EDGE,"E206");
            var Q125;
            Q125=sQuery(id+"F0.wireOp",EDGE,"E238");
            var Q126;
            Q126=sQuery(id+"F0.wireOp",EDGE,"E94");
            var Q127;
            Q127=sQuery(id+"F0.wireOp",EDGE,"E110");
            var Q128;
            Q128=sQuery(id+"F0.wireOp",EDGE,"E126");
            var Q129;
            Q129=sQuery(id+"F0.wireOp",EDGE,"E253");
            var Q130;
            Q130=sQuery(id+"F0.wireOp",EDGE,"E189");
            var Q131;
            Q131=sQuery(id+"F0.wireOp",EDGE,"E205");
            var Q132;
            Q132=sQuery(id+"F0.wireOp",EDGE,"E237");
            var Q133;
            Q133=sQuery(id+"F0.wireOp",EDGE,"E157");
            var Q134;
            Q134=sQuery(id+"F0.wireOp",EDGE,"E93");
            var Q135;
            Q135=sQuery(id+"F0.wireOp",EDGE,"E109");
            var Q136;
            Q136=sQuery(id+"F0.wireOp",EDGE,"E125");
            var Q137;
            Q137=sQuery(id+"F0.wireOp",EDGE,"E141");
            var Q138;
            Q138=sQuery(id+"F0.wireOp",EDGE,"E45");
            var Q139;
            Q139=sQuery(id+"F0.wireOp",EDGE,"E61");
            var Q140;
            Q140=sQuery(id+"F0.wireOp",EDGE,"E77");
            var Q141;
            Q141=sQuery(id+"F0.wireOp",EDGE,"E159");
            var Q142;
            Q142=sQuery(id+"F0.wireOp",EDGE,"E239");
            var Q143;
            Q143=sQuery(id+"F0.wireOp",EDGE,"E207");
            var Q144;
            Q144=sQuery(id+"F0.wireOp",EDGE,"E191");
            var Q145;
            Q145=sQuery(id+"F0.wireOp",EDGE,"E255");
            var Q146;
            Q146=sQuery(id+"F0.wireOp",EDGE,"E47");
            var Q147;
            Q147=sQuery(id+"F0.wireOp",EDGE,"E143");
            var Q148;
            Q148=sQuery(id+"F0.wireOp",EDGE,"E111");
            var Q149;
            Q149=sQuery(id+"F0.wireOp",EDGE,"E95");
            var Q150;
            Q150=sQuery(id+"F0.wireOp",EDGE,"E160");
            var Q151;
            Q151=sQuery(id+"F0.wireOp",EDGE,"E240");
            var Q152;
            Q152=sQuery(id+"F0.wireOp",EDGE,"E224");
            var Q153;
            Q153=sQuery(id+"F0.wireOp",EDGE,"E208");
            var Q154;
            Q154=sQuery(id+"F0.wireOp",EDGE,"E256");
            var Q155;
            Q155=sQuery(id+"F0.wireOp",EDGE,"E80");
            var Q156;
            Q156=sQuery(id+"F0.wireOp",EDGE,"E64");
            var Q157;
            Q157=sQuery(id+"F0.wireOp",EDGE,"E48");
            var Q158;
            Q158=sQuery(id+"F0.wireOp",EDGE,"E32");
            var Q159;
            Q159=sQuery(id+"F0.wireOp",EDGE,"E128");
            var Q160;
            Q160=sQuery(id+"F0.wireOp",EDGE,"E96");
            var Q161;
            Q161=sQuery(id+"F0.wireOp",EDGE,"E55");
            var Q162;
            Q162=sQuery(id+"F0.wireOp",EDGE,"E39");
            var Q163;
            Q163=sQuery(id+"F0.wireOp",EDGE,"E119");
            var Q164;
            Q164=sQuery(id+"F0.wireOp",EDGE,"E87");
            var Q165;
            Q165=sQuery(id+"F0.wireOp",EDGE,"E71");
            var Q166;
            Q166=sQuery(id+"F0.wireOp",EDGE,"E183");
            var Q167;
            Q167=sQuery(id+"F0.wireOp",EDGE,"E167");
            var Q168;
            Q168=sQuery(id+"F0.wireOp",EDGE,"E151");
            var Q169;
            Q169=sQuery(id+"F0.wireOp",EDGE,"E135");
            var Q170;
            Q170=sQuery(id+"F0.wireOp",EDGE,"E247");
            var Q171;
            Q171=sQuery(id+"F0.wireOp",EDGE,"E231");
            var Q172;
            Q172=sQuery(id+"F0.wireOp",EDGE,"E215");
            var Q173;
            Q173=sQuery(id+"F0.wireOp",EDGE,"E199");
            var Q174;
            Q174=sQuery(id+"F0.wireOp",EDGE,"E33");
            var Q175;
            Q175=sQuery(id+"F0.wireOp",EDGE,"E113");
            var Q176;
            Q176=sQuery(id+"F0.wireOp",EDGE,"E65");
            var Q177;
            Q177=sQuery(id+"F0.wireOp",EDGE,"E145");
            var Q178;
            Q178=sQuery(id+"F0.wireOp",EDGE,"E129");
            var Q179;
            Q179=sQuery(id+"F0.wireOp",EDGE,"E209");
            var Q180;
            Q180=sQuery(id+"F0.wireOp",EDGE,"E193");
            var Q181;
            Q181=sQuery(id+"F0.wireOp",EDGE,"E177");
            var Q182;
            Q182=sQuery(id+"F0.wireOp",EDGE,"E161");
            var Q183;
            Q183=sQuery(id+"F0.wireOp",EDGE,"E257");
            var Q184;
            Q184=sQuery(id+"F0.wireOp",EDGE,"E56");
            var Q185;
            Q185=sQuery(id+"F0.wireOp",EDGE,"E24");
            var Q186;
            Q186=sQuery(id+"F0.wireOp",EDGE,"E120");
            var Q187;
            Q187=sQuery(id+"F0.wireOp",EDGE,"E104");
            var Q188;
            Q188=sQuery(id+"F0.wireOp",EDGE,"E88");
            var Q189;
            Q189=sQuery(id+"F0.wireOp",EDGE,"E72");
            var Q190;
            Q190=sQuery(id+"F0.wireOp",EDGE,"E184");
            var Q191;
            Q191=sQuery(id+"F0.wireOp",EDGE,"E168");
            var Q192;
            Q192=sQuery(id+"F0.wireOp",EDGE,"E152");
            var Q193;
            Q193=sQuery(id+"F0.wireOp",EDGE,"E136");
            var Q194;
            Q194=sQuery(id+"F0.wireOp",EDGE,"E248");
            var Q195;
            Q195=sQuery(id+"F0.wireOp",EDGE,"E232");
            var Q196;
            Q196=sQuery(id+"F0.wireOp",EDGE,"E216");
            var Q197;
            Q197=sQuery(id+"F0.wireOp",EDGE,"E200");
            var Q198;
            Q198=sQuery(id+"F0.wireOp",EDGE,"E34");
            var Q199;
            Q199=sQuery(id+"F0.wireOp",EDGE,"E18");
            var Q200;
            Q200=sQuery(id+"F0.wireOp",EDGE,"E114");
            var Q201;
            Q201=sQuery(id+"F0.wireOp",EDGE,"E98");
            var Q202;
            Q202=sQuery(id+"F0.wireOp",EDGE,"E82");
            var Q203;
            Q203=sQuery(id+"F0.wireOp",EDGE,"E66");
            var Q204;
            Q204=sQuery(id+"F0.wireOp",EDGE,"E130");
            var Q205;
            Q205=sQuery(id+"F0.wireOp",EDGE,"E210");
            var Q206;
            Q206=sQuery(id+"F0.wireOp",EDGE,"E258");
            var Q207;
            Q207=sQuery(id+"F0.wireOp",EDGE,"E162");
            var Q208;
            Q208=sQuery(id+"F0.wireOp",EDGE,"E242");
            var Q209;
            Q209=sQuery(id+"F0.wireOp",EDGE,"E226");
            var Q210;
            Q210=sQuery(id+"F0.wireOp",EDGE,"E41");
            var Q211;
            Q211=sQuery(id+"F0.wireOp",EDGE,"E25");
            var Q212;
            Q212=sQuery(id+"F0.wireOp",EDGE,"E121");
            var Q213;
            Q213=sQuery(id+"F0.wireOp",EDGE,"E105");
            var Q214;
            Q214=sQuery(id+"F0.wireOp",EDGE,"E89");
            var Q215;
            Q215=sQuery(id+"F0.wireOp",EDGE,"E73");
            var Q216;
            Q216=sQuery(id+"F0.wireOp",EDGE,"E153");
            var Q217;
            Q217=sQuery(id+"F0.wireOp",EDGE,"E137");
            var Q218;
            Q218=sQuery(id+"F0.wireOp",EDGE,"E249");
            var Q219;
            Q219=sQuery(id+"F0.wireOp",EDGE,"E233");
            var Q220;
            Q220=sQuery(id+"F0.wireOp",EDGE,"E217");
            var Q221;
            Q221=sQuery(id+"F0.wireOp",EDGE,"E201");
            var Q222;
            Q222=sQuery(id+"F0.wireOp",EDGE,"E51");
            var Q223;
            Q223=sQuery(id+"F0.wireOp",EDGE,"E19");
            var Q224;
            Q224=sQuery(id+"F0.wireOp",EDGE,"E115");
            var Q225;
            Q225=sQuery(id+"F0.wireOp",EDGE,"E99");
            var Q226;
            Q226=sQuery(id+"F0.wireOp",EDGE,"E83");
            var Q227;
            Q227=sQuery(id+"F0.wireOp",EDGE,"E67");
            var Q228;
            Q228=sQuery(id+"F0.wireOp",EDGE,"E147");
            var Q229;
            Q229=sQuery(id+"F0.wireOp",EDGE,"E131");
            var Q230;
            Q230=sQuery(id+"F0.wireOp",EDGE,"E211");
            var Q231;
            Q231=sQuery(id+"F0.wireOp",EDGE,"E195");
            var Q232;
            Q232=sQuery(id+"F0.wireOp",EDGE,"E163");
            var Q233;
            Q233=sQuery(id+"F0.wireOp",EDGE,"E259");
            var Q234;
            Q234=sQuery(id+"F0.wireOp",EDGE,"E227");
            var Q235;
            Q235=sQuery(id+"F0.wireOp",EDGE,"E58");
            var Q236;
            Q236=sQuery(id+"F0.wireOp",EDGE,"E26");
            var Q237;
            Q237=sQuery(id+"F0.wireOp",EDGE,"E122");
            var Q238;
            Q238=sQuery(id+"F0.wireOp",EDGE,"E106");
            var Q239;
            Q239=sQuery(id+"F0.wireOp",EDGE,"E74");
            var Q240;
            Q240=sQuery(id+"F0.wireOp",EDGE,"E186");
            var Q241;
            Q241=sQuery(id+"F0.wireOp",EDGE,"E138");
            var Q242;
            Q242=sQuery(id+"F0.wireOp",EDGE,"E250");
            var Q243;
            Q243=sQuery(id+"F0.wireOp",EDGE,"E234");
            var Q244;
            Q244=sQuery(id+"F0.wireOp",EDGE,"E202");
            var Q245;
            Q245=sQuery(id+"F0.wireOp",EDGE,"E218");
            var Q246;
            Q246=sQuery(id+"F0.wireOp",EDGE,"E52");
            var Q247;
            Q247=sQuery(id+"F0.wireOp",EDGE,"E20");
            var Q248;
            Q248=sQuery(id+"F0.wireOp",EDGE,"E116");
            var Q249;
            Q249=sQuery(id+"F0.wireOp",EDGE,"E100");
            var Q250;
            Q250=sQuery(id+"F0.wireOp",EDGE,"E84");
            var Q251;
            Q251=sQuery(id+"F0.wireOp",EDGE,"E68");
            var Q252;
            Q252=sQuery(id+"F0.wireOp",EDGE,"E132");
            var Q253;
            Q253=sQuery(id+"F0.wireOp",EDGE,"E212");
            var Q254;
            Q254=sQuery(id+"F0.wireOp",EDGE,"E196");
            var Q255;
            Q255=sQuery(id+"F0.wireOp",EDGE,"E164");
            var Q256;
            Q256=sQuery(id+"F0.wireOp",EDGE,"E260");
            var Q257;
            Q257=sQuery(id+"F0.wireOp",EDGE,"E244");
            var Q258;
            Q258=sQuery(id+"F0.wireOp",EDGE,"E228");
            var Q259;
            Q259=sQuery(id+"F0.wireOp",EDGE,"E59");
            var Q260;
            Q260=sQuery(id+"F0.wireOp",EDGE,"E43");
            var Q261;
            Q261=sQuery(id+"F0.wireOp",EDGE,"E123");
            var Q262;
            Q262=sQuery(id+"F0.wireOp",EDGE,"E107");
            var Q263;
            Q263=sQuery(id+"F0.wireOp",EDGE,"E91");
            var Q264;
            Q264=sQuery(id+"F0.wireOp",EDGE,"E187");
            var Q265;
            Q265=sQuery(id+"F0.wireOp",EDGE,"E155");
            var Q266;
            Q266=sQuery(id+"F0.wireOp",EDGE,"E139");
            var Q267;
            Q267=sQuery(id+"F0.wireOp",EDGE,"E251");
            var Q268;
            Q268=sQuery(id+"F0.wireOp",EDGE,"E235");
            var Q269;
            Q269=sQuery(id+"F0.wireOp",EDGE,"E219");
            var Q270;
            Q270=sQuery(id+"F0.wireOp",EDGE,"E203");
            var Q271;
            Q271=sQuery(id+"F0.wireOp",EDGE,"E53");
            var Q272;
            Q272=sQuery(id+"F0.wireOp",EDGE,"E37");
            var Q273;
            Q273=sQuery(id+"F0.wireOp",EDGE,"E21");
            var Q274;
            Q274=sQuery(id+"F0.wireOp",EDGE,"E117");
            var Q275;
            Q275=sQuery(id+"F0.wireOp",EDGE,"E101");
            var Q276;
            Q276=sQuery(id+"F0.wireOp",EDGE,"E85");
            var Q277;
            Q277=sQuery(id+"F0.wireOp",EDGE,"E69");
            var Q278;
            Q278=sQuery(id+"F0.wireOp",EDGE,"E149");
            var Q279;
            Q279=sQuery(id+"F0.wireOp",EDGE,"E133");
            var Q280;
            Q280=sQuery(id+"F0.wireOp",EDGE,"E181");
            var Q281;
            Q281=sQuery(id+"F0.wireOp",EDGE,"E165");
            var Q282;
            Q282=sQuery(id+"F0.wireOp",EDGE,"E261");
            var Q283;
            Q283=sQuery(id+"F0.wireOp",EDGE,"E229");
            var Q284;
            Q284=sQuery(id+"F0.wireOp",EDGE,"E60");
            var Q285;
            Q285=sQuery(id+"F0.wireOp",EDGE,"E28");
            var Q286;
            Q286=sQuery(id+"F0.wireOp",EDGE,"E124");
            var Q287;
            Q287=sQuery(id+"F0.wireOp",EDGE,"E108");
            var Q288;
            Q288=sQuery(id+"F0.wireOp",EDGE,"E92");
            var Q289;
            Q289=sQuery(id+"F0.wireOp",EDGE,"E188");
            var Q290;
            Q290=sQuery(id+"F0.wireOp",EDGE,"E172");
            var Q291;
            Q291=sQuery(id+"F0.wireOp",EDGE,"E140");
            var Q292;
            Q292=sQuery(id+"F0.wireOp",EDGE,"E252");
            var Q293;
            Q293=sQuery(id+"F0.wireOp",EDGE,"E236");
            var Q294;
            Q294=sQuery(id+"F0.wireOp",EDGE,"E220");
            var Q295;
            Q295=sQuery(id+"F0.wireOp",EDGE,"E204");
            var Q296;
            Q296=sQuery(id+"F0.wireOp",EDGE,"E54");
            var Q297;
            Q297=sQuery(id+"F0.wireOp",EDGE,"E22");
            var Q298;
            Q298=sQuery(id+"F0.wireOp",EDGE,"E118");
            var Q299;
            Q299=sQuery(id+"F0.wireOp",EDGE,"E86");
            var Q300;
            Q300=sQuery(id+"F0.wireOp",EDGE,"E70");
            var Q301;
            Q301=sQuery(id+"F0.wireOp",EDGE,"E150");
            var Q302;
            Q302=sQuery(id+"F0.wireOp",EDGE,"E134");
            var Q303;
            Q303=sQuery(id+"F0.wireOp",EDGE,"E214");
            var Q304;
            Q304=sQuery(id+"F0.wireOp",EDGE,"E198");
            var Q305;
            Q305=sQuery(id+"F0.wireOp",EDGE,"E182");
            var Q306;
            Q306=sQuery(id+"F0.wireOp",EDGE,"E166");
            var Q307;
            Q307=sQuery(id+"F0.wireOp",EDGE,"E246");
            var Q308;
            Q308=sQuery(id+"F0.wireOp",EDGE,"E230");
            var Q309;
            Q309=sQuery(id+"F0.wireOp",EDGE,"E14");
            var Q310;
            Q310=sQuery(id+"F0.wireOp",EDGE,"E15");
            var Q311;
            Q311=sQuery(id+"F0.wireOp",EDGE,"E0");
            var Q312;
            Q312=sQuery(id+"F0.wireOp",EDGE,"E1");
            var Q313;
            Q313=sQuery(id+"F0.wireOp",EDGE,"E2");
            var Q314;
            Q314=sQuery(id+"F0.wireOp",EDGE,"E3");
            var Q315;
            Q315=sQuery(id+"F0.wireOp",EDGE,"E4");
            var Q316;
            Q316=sQuery(id+"F0.wireOp",EDGE,"E7");
            var Q317;
            Q317=sQuery(id+"F0.wireOp",EDGE,"E8");
            var Q318;
            Q318=sQuery(id+"F0.wireOp",EDGE,"E10");
            var Q319;
            Q319=sQuery(id+"F0.wireOp",EDGE,"E12");
            var Q320;
            Q320=sQuery(id+"F0.wireOp",EDGE,"E60");
            var Q321;
            Q321=sQuery(id+"F0.wireOp",EDGE,"E226");
            var Q322;
            Q322=sQuery(id+"F0.wireOp",EDGE,"E242");
            var Q323;
            Q323=sQuery(id+"F0.wireOp",EDGE,"E258");
            var Q324;
            Q324=sQuery(id+"F0.wireOp",EDGE,"E12");
            var Q325;
            Q325=sQuery(id+"F0.wireOp",EDGE,"E113");
            var Q326;
            Q326=sQuery(id+"F0.wireOp",EDGE,"E129");
            var Q327;
            Q327=sQuery(id+"F0.wireOp",EDGE,"E145");
            var Q328;
            Q328=sQuery(id+"F0.wireOp",EDGE,"E33");
            var Q329;
            Q329=sQuery(id+"F0.wireOp",EDGE,"E65");
            var Q330;
            Q330=sQuery(id+"F0.wireOp",EDGE,"E187");
            var Q331;
            Q331=sQuery(id+"F0.wireOp",EDGE,"E251");
            var Q332;
            Q332=sQuery(id+"F0.wireOp",EDGE,"E235");
            var Q333;
            Q333=sQuery(id+"F0.wireOp",EDGE,"E203");
            var Q334;
            Q334=sQuery(id+"F0.wireOp",EDGE,"E219");
            var Q335;
            Q335=sQuery(id+"F0.wireOp",EDGE,"E155");
            var Q336;
            Q336=sQuery(id+"F0.wireOp",EDGE,"E91");
            var Q337;
            Q337=sQuery(id+"F0.wireOp",EDGE,"E107");
            var Q338;
            Q338=sQuery(id+"F0.wireOp",EDGE,"E123");
            var Q339;
            Q339=sQuery(id+"F0.wireOp",EDGE,"E139");
            var Q340;
            Q340=sQuery(id+"F0.wireOp",EDGE,"E43");
            var Q341;
            Q341=sQuery(id+"F0.wireOp",EDGE,"E59");
            var Q342;
            Q342=sQuery(id+"F0.wireOp",EDGE,"E257");
            var Q343;
            Q343=sQuery(id+"F0.wireOp",EDGE,"E161");
            var Q344;
            Q344=sQuery(id+"F0.wireOp",EDGE,"E177");
            var Q345;
            Q345=sQuery(id+"F0.wireOp",EDGE,"E193");
            var Q346;
            Q346=sQuery(id+"F0.wireOp",EDGE,"E209");
            var Q347;
            Q347=sQuery(id+"F0.wireOp",EDGE,"E250");
            var Q348;
            Q348=sQuery(id+"F0.wireOp",EDGE,"E32");
            var Q349;
            Q349=sQuery(id+"F0.wireOp",EDGE,"E48");
            var Q350;
            Q350=sQuery(id+"F0.wireOp",EDGE,"E64");
            var Q351;
            Q351=sQuery(id+"F0.wireOp",EDGE,"E80");
            var Q352;
            Q352=sQuery(id+"F0.wireOp",EDGE,"E186");
            var Q353;
            Q353=sQuery(id+"F0.wireOp",EDGE,"E218");
            var Q354;
            Q354=sQuery(id+"F0.wireOp",EDGE,"E202");
            var Q355;
            Q355=sQuery(id+"F0.wireOp",EDGE,"E234");
            var Q356;
            Q356=sQuery(id+"F0.wireOp",EDGE,"E106");
            var Q357;
            Q357=sQuery(id+"F0.wireOp",EDGE,"E122");
            var Q358;
            Q358=sQuery(id+"F0.wireOp",EDGE,"E138");
            var Q359;
            Q359=sQuery(id+"F0.wireOp",EDGE,"E26");
            var Q360;
            Q360=sQuery(id+"F0.wireOp",EDGE,"E58");
            var Q361;
            Q361=sQuery(id+"F0.wireOp",EDGE,"E74");
            var Q362;
            Q362=sQuery(id+"F0.wireOp",EDGE,"E224");
            var Q363;
            Q363=sQuery(id+"F0.wireOp",EDGE,"E240");
            var Q364;
            Q364=sQuery(id+"F0.wireOp",EDGE,"E256");
            var Q365;
            Q365=sQuery(id+"F0.wireOp",EDGE,"E10");
            var Q366;
            Q366=sQuery(id+"F0.wireOp",EDGE,"E160");
            var Q367;
            Q367=sQuery(id+"F0.wireOp",EDGE,"E208");
            var Q368;
            Q368=sQuery(id+"F0.wireOp",EDGE,"E96");
            var Q369;
            Q369=sQuery(id+"F0.wireOp",EDGE,"E128");
            var Q370;
            Q370=sQuery(id+"F0.wireOp",EDGE,"E153");
            var Q371;
            Q371=sQuery(id+"F0.wireOp",EDGE,"E89");
            var Q372;
            Q372=sQuery(id+"F0.wireOp",EDGE,"E105");
            var Q373;
            Q373=sQuery(id+"F0.wireOp",EDGE,"E121");
            var Q374;
            Q374=sQuery(id+"F0.wireOp",EDGE,"E137");
            var Q375;
            Q375=sQuery(id+"F0.wireOp",EDGE,"E25");
            var Q376;
            Q376=sQuery(id+"F0.wireOp",EDGE,"E41");
            var Q377;
            Q377=sQuery(id+"F0.wireOp",EDGE,"E73");
            var Q378;
            Q378=sQuery(id+"F0.wireOp",EDGE,"E239");
            var Q379;
            Q379=sQuery(id+"F0.wireOp",EDGE,"E255");
            var Q380;
            Q380=sQuery(id+"F0.wireOp",EDGE,"E159");
            var Q381;
            Q381=sQuery(id+"F0.wireOp",EDGE,"E191");
            var Q382;
            Q382=sQuery(id+"F0.wireOp",EDGE,"E207");
            var Q383;
            Q383=sQuery(id+"F0.wireOp",EDGE,"E95");
            var Q384;
            Q384=sQuery(id+"F0.wireOp",EDGE,"E111");
            var Q385;
            Q385=sQuery(id+"F0.wireOp",EDGE,"E143");
            var Q386;
            Q386=sQuery(id+"F0.wireOp",EDGE,"E47");
            var Q387;
            Q387=sQuery(id+"F0.wireOp",EDGE,"E249");
            var Q388;
            Q388=sQuery(id+"F0.wireOp",EDGE,"E201");
            var Q389;
            Q389=sQuery(id+"F0.wireOp",EDGE,"E217");
            var Q390;
            Q390=sQuery(id+"F0.wireOp",EDGE,"E233");
            var Q391;
            Q391=sQuery(id+"F0.wireOp",EDGE,"E88");
            var Q392;
            Q392=sQuery(id+"F0.wireOp",EDGE,"E104");
            var Q393;
            Q393=sQuery(id+"F0.wireOp",EDGE,"E120");
            var Q394;
            Q394=sQuery(id+"F0.wireOp",EDGE,"E136");
            var Q395;
            Q395=sQuery(id+"F0.wireOp",EDGE,"E24");
            var Q396;
            Q396=sQuery(id+"F0.wireOp",EDGE,"E56");
            var Q397;
            Q397=sQuery(id+"F0.wireOp",EDGE,"E72");
            var Q398;
            Q398=sQuery(id+"F0.wireOp",EDGE,"E222");
            var Q399;
            Q399=sQuery(id+"F0.wireOp",EDGE,"E238");
            var Q400;
            Q400=sQuery(id+"F0.wireOp",EDGE,"E254");
            var Q401;
            Q401=sQuery(id+"F0.wireOp",EDGE,"E8");
            var Q402;
            Q402=sQuery(id+"F0.wireOp",EDGE,"E206");
            var Q403;
            Q403=sQuery(id+"F0.wireOp",EDGE,"E94");
            var Q404;
            Q404=sQuery(id+"F0.wireOp",EDGE,"E110");
            var Q405;
            Q405=sQuery(id+"F0.wireOp",EDGE,"E126");
            var Q406;
            Q406=sQuery(id+"F0.wireOp",EDGE,"E30");
            var Q407;
            Q407=sQuery(id+"F0.wireOp",EDGE,"E62");
            var Q408;
            Q408=sQuery(id+"F0.wireOp",EDGE,"E78");
            var Q409;
            Q409=sQuery(id+"F0.wireOp",EDGE,"E248");
            var Q410;
            Q410=sQuery(id+"F0.wireOp",EDGE,"E184");
            var Q411;
            Q411=sQuery(id+"F0.wireOp",EDGE,"E200");
            var Q412;
            Q412=sQuery(id+"F0.wireOp",EDGE,"E216");
            var Q413;
            Q413=sQuery(id+"F0.wireOp",EDGE,"E232");
            var Q414;
            Q414=sQuery(id+"F0.wireOp",EDGE,"E168");
            var Q415;
            Q415=sQuery(id+"F0.wireOp",EDGE,"E152");
            var Q416;
            Q416=sQuery(id+"F0.wireOp",EDGE,"E228");
            var Q417;
            Q417=sQuery(id+"F0.wireOp",EDGE,"E39");
            var Q418;
            Q418=sQuery(id+"F0.wireOp",EDGE,"E244");
            var Q419;
            Q419=sQuery(id+"F0.wireOp",EDGE,"E55");
            var Q420;
            Q420=sQuery(id+"F0.wireOp",EDGE,"E71");
            var Q421;
            Q421=sQuery(id+"F0.wireOp",EDGE,"E260");
            var Q422;
            Q422=sQuery(id+"F0.wireOp",EDGE,"E14");
            var Q423;
            Q423=sQuery(id+"F0.wireOp",EDGE,"E164");
            var Q424;
            Q424=sQuery(id+"F0.wireOp",EDGE,"E196");
            var Q425;
            Q425=sQuery(id+"F0.wireOp",EDGE,"E212");
            var Q426;
            Q426=sQuery(id+"F0.wireOp",EDGE,"E100");
            var Q427;
            Q427=sQuery(id+"F0.wireOp",EDGE,"E116");
            var Q428;
            Q428=sQuery(id+"F0.wireOp",EDGE,"E132");
            var Q429;
            Q429=sQuery(id+"F0.wireOp",EDGE,"E52");
            var Q430;
            Q430=sQuery(id+"F0.wireOp",EDGE,"E237");
            var Q431;
            Q431=sQuery(id+"F0.wireOp",EDGE,"E253");
            var Q432;
            Q432=sQuery(id+"F0.wireOp",EDGE,"E157");
            var Q433;
            Q433=sQuery(id+"F0.wireOp",EDGE,"E7");
            var Q434;
            Q434=sQuery(id+"F0.wireOp",EDGE,"E189");
            var Q435;
            Q435=sQuery(id+"F0.wireOp",EDGE,"E205");
            var Q436;
            Q436=sQuery(id+"F0.wireOp",EDGE,"E93");
            var Q437;
            Q437=sQuery(id+"F0.wireOp",EDGE,"E109");
            var Q438;
            Q438=sQuery(id+"F0.wireOp",EDGE,"E125");
            var Q439;
            Q439=sQuery(id+"F0.wireOp",EDGE,"E141");
            var Q440;
            Q440=sQuery(id+"F0.wireOp",EDGE,"E68");
            var Q441;
            Q441=sQuery(id+"F0.wireOp",EDGE,"E84");
            var Q442;
            Q442=sQuery(id+"F0.wireOp",EDGE,"E20");
            var Q443;
            Q443=sQuery(id+"F0.wireOp",EDGE,"E45");
            var Q444;
            Q444=sQuery(id+"F0.wireOp",EDGE,"E61");
            var Q445;
            Q445=sQuery(id+"F0.wireOp",EDGE,"E77");
            var Q446;
            Q446=sQuery(id+"F0.wireOp",EDGE,"E247");
            var Q447;
            Q447=sQuery(id+"F0.wireOp",EDGE,"E183");
            var Q448;
            Q448=sQuery(id+"F0.wireOp",EDGE,"E199");
            var Q449;
            Q449=sQuery(id+"F0.wireOp",EDGE,"E215");
            var Q450;
            Q450=sQuery(id+"F0.wireOp",EDGE,"E231");
            var Q451;
            Q451=sQuery(id+"F0.wireOp",EDGE,"E167");
            var Q452;
            Q452=sQuery(id+"F0.wireOp",EDGE,"E151");
            var Q453;
            Q453=sQuery(id+"F0.wireOp",EDGE,"E227");
            var Q454;
            Q454=sQuery(id+"F0.wireOp",EDGE,"E259");
            var Q455;
            Q455=sQuery(id+"F0.wireOp",EDGE,"E163");
            var Q456;
            Q456=sQuery(id+"F0.wireOp",EDGE,"E87");
            var Q457;
            Q457=sQuery(id+"F0.wireOp",EDGE,"E119");
            var Q458;
            Q458=sQuery(id+"F0.wireOp",EDGE,"E135");
            var Q459;
            Q459=sQuery(id+"F0.wireOp",EDGE,"E195");
            var Q460;
            Q460=sQuery(id+"F0.wireOp",EDGE,"E211");
            var Q461;
            Q461=sQuery(id+"F0.wireOp",EDGE,"E115");
            var Q462;
            Q462=sQuery(id+"F0.wireOp",EDGE,"E99");
            var Q463;
            Q463=sQuery(id+"F0.wireOp",EDGE,"E131");
            var Q464;
            Q464=sQuery(id+"F0.wireOp",EDGE,"E147");
            var Q465;
            Q465=sQuery(id+"F0.wireOp",EDGE,"E51");
            var Q466;
            Q466=sQuery(id+"F0.wireOp",EDGE,"E67");
            var Q467;
            Q467=sQuery(id+"F0.wireOp",EDGE,"E83");
            var Q468;
            Q468=sQuery(id+"F0.wireOp",EDGE,"E19");
            var Q469;
            Q469=sQuery(id+"F0.wireOp",EDGE,"E173");
            var Q470;
            Q470=sQuery(id+"F0.wireOp",EDGE,"E162");
            var Q471;
            Q471=sQuery(id+"F0.wireOp",EDGE,"E210");
            var Q472;
            Q472=sQuery(id+"F0.wireOp",EDGE,"E98");
            var Q473;
            Q473=sQuery(id+"F0.wireOp",EDGE,"E114");
            var Q474;
            Q474=sQuery(id+"F0.wireOp",EDGE,"E130");
            var Q475;
            Q475=sQuery(id+"F0.wireOp",EDGE,"E34");
            var Q476;
            Q476=sQuery(id+"F0.wireOp",EDGE,"E66");
            var Q477;
            Q477=sQuery(id+"F0.wireOp",EDGE,"E82");
            var Q478;
            Q478=sQuery(id+"F0.wireOp",EDGE,"E18");
            var Q479;
            Q479=sQuery(id+"F0.wireOp",EDGE,"E252");
            var Q480;
            Q480=sQuery(id+"F0.wireOp",EDGE,"E188");
            var Q481;
            Q481=sQuery(id+"F0.wireOp",EDGE,"E204");
            var Q482;
            Q482=sQuery(id+"F0.wireOp",EDGE,"E220");
            var Q483;
            Q483=sQuery(id+"F0.wireOp",EDGE,"E236");
            var Q484;
            Q484=sQuery(id+"F0.wireOp",EDGE,"E172");
            var Q485;
            Q485=sQuery(id+"F0.wireOp",EDGE,"E92");
            var Q486;
            Q486=sQuery(id+"F0.wireOp",EDGE,"E108");
            var Q487;
            Q487=sQuery(id+"F0.wireOp",EDGE,"E124");
            var Q488;
            Q488=sQuery(id+"F0.wireOp",EDGE,"E140");
            var Q489;
            Q489=sQuery(id+"F0.wireOp",EDGE,"E28");
            var Q490;
            Q490=sQuery(id+"F0.wireOp",EDGE,"E21");
            var Q491;
            Q491=sQuery(id+"F0.wireOp",EDGE,"E85");
            var Q492;
            Q492=sQuery(id+"F0.wireOp",EDGE,"E69");
            var Q493;
            Q493=sQuery(id+"F0.wireOp",EDGE,"E53");
            var Q494;
            Q494=sQuery(id+"F0.wireOp",EDGE,"E37");
            var Q495;
            Q495=sQuery(id+"F0.wireOp",EDGE,"E149");
            var Q496;
            Q496=sQuery(id+"F0.wireOp",EDGE,"E133");
            var Q497;
            Q497=sQuery(id+"F0.wireOp",EDGE,"E117");
            var Q498;
            Q498=sQuery(id+"F0.wireOp",EDGE,"E101");
            var Q499;
            Q499=sQuery(id+"F0.wireOp",EDGE,"E181");
            var Q500;
            Q500=sQuery(id+"F0.wireOp",EDGE,"E165");
            var Q501;
            Q501=sQuery(id+"F0.wireOp",EDGE,"E15");
            var Q502;
            Q502=sQuery(id+"F0.wireOp",EDGE,"E261");
            var Q503;
            Q503=sQuery(id+"F0.wireOp",EDGE,"E229");
            var Q504;
            Q504=sQuery(id+"F0.wireOp",EDGE,"E22");
            var Q505;
            Q505=sQuery(id+"F0.wireOp",EDGE,"E86");
            var Q506;
            Q506=sQuery(id+"F0.wireOp",EDGE,"E70");
            var Q507;
            Q507=sQuery(id+"F0.wireOp",EDGE,"E54");
            var Q508;
            Q508=sQuery(id+"F0.wireOp",EDGE,"E150");
            var Q509;
            Q509=sQuery(id+"F0.wireOp",EDGE,"E134");
            var Q510;
            Q510=sQuery(id+"F0.wireOp",EDGE,"E118");
            var Q511;
            Q511=sQuery(id+"F0.wireOp",EDGE,"E214");
            var Q512;
            Q512=sQuery(id+"F0.wireOp",EDGE,"E198");
            var Q513;
            Q513=sQuery(id+"F0.wireOp",EDGE,"E182");
            var Q514;
            Q514=sQuery(id+"F0.wireOp",EDGE,"E166");
            var Q515;
            Q515=sQuery(id+"F0.wireOp",EDGE,"E0");
            var Q516;
            Q516=sQuery(id+"F0.wireOp",EDGE,"E246");
            var Q517;
            Q517=sQuery(id+"F0.wireOp",EDGE,"E230");
            var Q518;
            Q518=sQuery(id+"F0.wireOp",EDGE,"E103");
            var Q519;
            Q519=sQuery(id+"F0.wireOp",EDGE,"E1");
            var Q520;
            Q520=sQuery(id+"F0.wireOp",EDGE,"E2");
            var Q521;
            Q521=sQuery(id+"F0.wireOp",EDGE,"E3");
            var Q522;
            Q522=sQuery(id+"F0.wireOp",EDGE,"E4");
            var Q523;
            Q523=sQuery(id+"F0.wireOp",EDGE,"E173");
            var Q524;
            Q524=sQuery(id+"F0.wireOp",EDGE,"E103");
            var Q525;
            Q525=sQuery(id+"F0.wireOp",EDGE,"E102");
            var Q526;
            Q526=sQuery(id+"F0.wireOp",EDGE,"E102");
            extrude(context, id + "F1", {"entities" : qUnion([Q0, Q1, Q2, Q3, Q4]), "surfaceEntities" : qUnion([Q5, Q6, Q7, Q8, Q9, Q10, Q11, Q12, Q13, Q14, Q15, Q16, Q17, Q18, Q19, Q20, Q21, Q22, Q23, Q24, Q25, Q26, Q27, Q28, Q29, Q30, Q31, Q32, Q33, Q34, Q35, Q36, Q37, Q38, Q39, Q40, Q41, Q42, Q43, Q44, Q45, Q46, Q47, Q48, Q49, Q50, Q51, Q52, Q53, Q54, Q55, Q56, Q57, Q58, Q59, Q60, Q61, Q62, Q63, Q64, Q65, Q66, Q67, Q68, Q69, Q70, Q71, Q72, Q73, Q74, Q75, Q76, Q77, Q78, Q79, Q80, Q81, Q82, Q83, Q84, Q85, Q86, Q87, Q88, Q89, Q90, Q91, Q92, Q93, Q94, Q95, Q96, Q97, Q98, Q99, Q100, Q101, Q102, Q103, Q104, Q105, Q106, Q107, Q108, Q109, Q110, Q111, Q112, Q113, Q114, Q115, Q116, Q117, Q118, Q119, Q120, Q121, Q122, Q123, Q124, Q125, Q126, Q127, Q128, Q129, Q130, Q131, Q132, Q133, Q134, Q135, Q136, Q137, Q138, Q139, Q140, Q141, Q142, Q143, Q144, Q145, Q146, Q147, Q148, Q149, Q150, Q151, Q152, Q153, Q154, Q155, Q156, Q157, Q158, Q159, Q160, Q161, Q162, Q163, Q164, Q165, Q166, Q167, Q168, Q169, Q170, Q171, Q172, Q173, Q174, Q175, Q176, Q177, Q178, Q179, Q180, Q181, Q182, Q183, Q184, Q185, Q186, Q187, Q188, Q189, Q190, Q191, Q192, Q193, Q194, Q195, Q196, Q197, Q198, Q199, Q200, Q201, Q202, Q203, Q204, Q205, Q206, Q207, Q208, Q209, Q210, Q211, Q212, Q213, Q214, Q215, Q216, Q217, Q218, Q219, Q220, Q221, Q222, Q223, Q224, Q225, Q226, Q227, Q228, Q229, Q230, Q231, Q232, Q233, Q234, Q235, Q236, Q237, Q238, Q239, Q240, Q241, Q242, Q243, Q244, Q245, Q246, Q247, Q248, Q249, Q250, Q251, Q252, Q253, Q254, Q255, Q256, Q257, Q258, Q259, Q260, Q261, Q262, Q263, Q264, Q265, Q266, Q267, Q268, Q269, Q270, Q271, Q272, Q273, Q274, Q275, Q276, Q277, Q278, Q279, Q280, Q281, Q282, Q283, Q284, Q285, Q286, Q287, Q288, Q289, Q290, Q291, Q292, Q293, Q294, Q295, Q296, Q297, Q298, Q299, Q300, Q301, Q302, Q303, Q304, Q305, Q306, Q307, Q308, Q309, Q310, Q311, Q312, Q313, Q314, Q315, Q316, Q317, Q318, Q319, Q320, Q321, Q322, Q323, Q324, Q325, Q326, Q327, Q328, Q329, Q330, Q331, Q332, Q333, Q334, Q335, Q336, Q337, Q338, Q339, Q340, Q341, Q342, Q343, Q344, Q345, Q346, Q347, Q348, Q349, Q350, Q351, Q352, Q353, Q354, Q355, Q356, Q357, Q358, Q359, Q360, Q361, Q362, Q363, Q364, Q365, Q366, Q367, Q368, Q369, Q370, Q371, Q372, Q373, Q374, Q375, Q376, Q377, Q378, Q379, Q380, Q381, Q382, Q383, Q384, Q385, Q386, Q387, Q388, Q389, Q390, Q391, Q392, Q393, Q394, Q395, Q396, Q397, Q398, Q399, Q400, Q401, Q402, Q403, Q404, Q405, Q406, Q407, Q408, Q409, Q410, Q411, Q412, Q413, Q414, Q415, Q416, Q417, Q418, Q419, Q420, Q421, Q422, Q423, Q424, Q425, Q426, Q427, Q428, Q429, Q430, Q431, Q432, Q433, Q434, Q435, Q436, Q437, Q438, Q439, Q440, Q441, Q442, Q443, Q444, Q445, Q446, Q447, Q448, Q449, Q450, Q451, Q452, Q453, Q454, Q455, Q456, Q457, Q458, Q459, Q460, Q461, Q462, Q463, Q464, Q465, Q466, Q467, Q468, Q469, Q470, Q471, Q472, Q473, Q474, Q475, Q476, Q477, Q478, Q479, Q480, Q481, Q482, Q483, Q484, Q485, Q486, Q487, Q488, Q489, Q490, Q491, Q492, Q493, Q494, Q495, Q496, Q497, Q498, Q499, Q500, Q501, Q502, Q503, Q504, Q505, Q506, Q507, Q508, Q509, Q510, Q511, Q512, Q513, Q514, Q515, Q516, Q517, Q518, Q519, Q520, Q521, Q522, Q523, Q524, Q525, Q526]), "depth" : (5 / 0.06) * mm});
        }
        {
            var Q0;
            Q0=makeQuery(id+"F1.opExtrude","SWEPT_BODY",BODY,{"disambiguationData":[OSD([sQuery(id+"F0.wireOp",EDGE,"E44"),sQuery(id+"F0.wireOp",EDGE,"E45"),sQuery(id+"F0.wireOp",EDGE,"E46"),sQuery(id+"F0.wireOp",EDGE,"E47"),sQuery(id+"F0.wireOp",EDGE,"E48"),sQuery(id+"F0.wireOp",EDGE,"E49"),sQuery(id+"F0.wireOp",EDGE,"E50"),sQuery(id+"F0.wireOp",EDGE,"E51"),sQuery(id+"F0.wireOp",EDGE,"E52"),sQuery(id+"F0.wireOp",EDGE,"E53"),sQuery(id+"F0.wireOp",EDGE,"E54"),sQuery(id+"F0.wireOp",EDGE,"E55"),sQuery(id+"F0.wireOp",EDGE,"E56"),sQuery(id+"F0.wireOp",EDGE,"E57"),sQuery(id+"F0.wireOp",EDGE,"E58"),sQuery(id+"F0.wireOp",EDGE,"E59"),sQuery(id+"F0.wireOp",EDGE,"E60"),sQuery(id+"F0.wireOp",EDGE,"E61"),sQuery(id+"F0.wireOp",EDGE,"E62"),sQuery(id+"F0.wireOp",EDGE,"E63"),sQuery(id+"F0.wireOp",EDGE,"E64"),sQuery(id+"F0.wireOp",EDGE,"E65"),sQuery(id+"F0.wireOp",EDGE,"E66"),sQuery(id+"F0.wireOp",EDGE,"E67"),sQuery(id+"F0.wireOp",EDGE,"E68"),sQuery(id+"F0.wireOp",EDGE,"E69"),sQuery(id+"F0.wireOp",EDGE,"E70"),sQuery(id+"F0.wireOp",EDGE,"E71"),sQuery(id+"F0.wireOp",EDGE,"E72"),sQuery(id+"F0.wireOp",EDGE,"E73"),sQuery(id+"F0.wireOp",EDGE,"E74"),sQuery(id+"F0.wireOp",EDGE,"E75"),sQuery(id+"F0.wireOp",EDGE,"E76"),sQuery(id+"F0.wireOp",EDGE,"E77"),sQuery(id+"F0.wireOp",EDGE,"E78"),sQuery(id+"F0.wireOp",EDGE,"E79"),sQuery(id+"F0.wireOp",EDGE,"E80"),sQuery(id+"F0.wireOp",EDGE,"E81"),sQuery(id+"F0.wireOp",EDGE,"E82"),sQuery(id+"F0.wireOp",EDGE,"E83"),sQuery(id+"F0.wireOp",EDGE,"E84"),sQuery(id+"F0.wireOp",EDGE,"E85"),sQuery(id+"F0.wireOp",EDGE,"E86"),sQuery(id+"F0.wireOp",EDGE,"E87"),sQuery(id+"F0.wireOp",EDGE,"E88"),sQuery(id+"F0.wireOp",EDGE,"E89"),sQuery(id+"F0.wireOp",EDGE,"E267")])]});
            var Q1;
            Q1=makeQuery(id+"F1.opExtrude","SWEPT_BODY",BODY,{"disambiguationData":[OSD([sQuery(id+"F0.wireOp",EDGE,"E0"),sQuery(id+"F0.wireOp",EDGE,"E1"),sQuery(id+"F0.wireOp",EDGE,"E2"),sQuery(id+"F0.wireOp",EDGE,"E3"),sQuery(id+"F0.wireOp",EDGE,"E4"),sQuery(id+"F0.wireOp",EDGE,"E5"),sQuery(id+"F0.wireOp",EDGE,"E6"),sQuery(id+"F0.wireOp",EDGE,"E7"),sQuery(id+"F0.wireOp",EDGE,"E8"),sQuery(id+"F0.wireOp",EDGE,"E9"),sQuery(id+"F0.wireOp",EDGE,"E10"),sQuery(id+"F0.wireOp",EDGE,"E11"),sQuery(id+"F0.wireOp",EDGE,"E12"),sQuery(id+"F0.wireOp",EDGE,"E13"),sQuery(id+"F0.wireOp",EDGE,"E14"),sQuery(id+"F0.wireOp",EDGE,"E15"),sQuery(id+"F0.wireOp",EDGE,"E16"),sQuery(id+"F0.wireOp",EDGE,"E17"),sQuery(id+"F0.wireOp",EDGE,"E18"),sQuery(id+"F0.wireOp",EDGE,"E19"),sQuery(id+"F0.wireOp",EDGE,"E20"),sQuery(id+"F0.wireOp",EDGE,"E21"),sQuery(id+"F0.wireOp",EDGE,"E22"),sQuery(id+"F0.wireOp",EDGE,"E23"),sQuery(id+"F0.wireOp",EDGE,"E24"),sQuery(id+"F0.wireOp",EDGE,"E25"),sQuery(id+"F0.wireOp",EDGE,"E26"),sQuery(id+"F0.wireOp",EDGE,"E27"),sQuery(id+"F0.wireOp",EDGE,"E28"),sQuery(id+"F0.wireOp",EDGE,"E29"),sQuery(id+"F0.wireOp",EDGE,"E30"),sQuery(id+"F0.wireOp",EDGE,"E31"),sQuery(id+"F0.wireOp",EDGE,"E32"),sQuery(id+"F0.wireOp",EDGE,"E33"),sQuery(id+"F0.wireOp",EDGE,"E34"),sQuery(id+"F0.wireOp",EDGE,"E35"),sQuery(id+"F0.wireOp",EDGE,"E36"),sQuery(id+"F0.wireOp",EDGE,"E37"),sQuery(id+"F0.wireOp",EDGE,"E38"),sQuery(id+"F0.wireOp",EDGE,"E39"),sQuery(id+"F0.wireOp",EDGE,"E40"),sQuery(id+"F0.wireOp",EDGE,"E41"),sQuery(id+"F0.wireOp",EDGE,"E42"),sQuery(id+"F0.wireOp",EDGE,"E43"),sQuery(id+"F0.wireOp",EDGE,"E266")])]});
            var Q2;
            Q2=makeQuery(id+"F1.opExtrude","SWEPT_BODY",BODY,{"disambiguationData":[OSD([sQuery(id+"F0.wireOp",EDGE,"E206"),sQuery(id+"F0.wireOp",EDGE,"E207"),sQuery(id+"F0.wireOp",EDGE,"E208"),sQuery(id+"F0.wireOp",EDGE,"E209"),sQuery(id+"F0.wireOp",EDGE,"E210"),sQuery(id+"F0.wireOp",EDGE,"E211"),sQuery(id+"F0.wireOp",EDGE,"E212"),sQuery(id+"F0.wireOp",EDGE,"E213"),sQuery(id+"F0.wireOp",EDGE,"E214"),sQuery(id+"F0.wireOp",EDGE,"E215"),sQuery(id+"F0.wireOp",EDGE,"E216"),sQuery(id+"F0.wireOp",EDGE,"E217"),sQuery(id+"F0.wireOp",EDGE,"E218"),sQuery(id+"F0.wireOp",EDGE,"E219"),sQuery(id+"F0.wireOp",EDGE,"E220"),sQuery(id+"F0.wireOp",EDGE,"E221"),sQuery(id+"F0.wireOp",EDGE,"E222"),sQuery(id+"F0.wireOp",EDGE,"E223"),sQuery(id+"F0.wireOp",EDGE,"E224"),sQuery(id+"F0.wireOp",EDGE,"E225"),sQuery(id+"F0.wireOp",EDGE,"E226"),sQuery(id+"F0.wireOp",EDGE,"E227"),sQuery(id+"F0.wireOp",EDGE,"E228"),sQuery(id+"F0.wireOp",EDGE,"E229"),sQuery(id+"F0.wireOp",EDGE,"E230"),sQuery(id+"F0.wireOp",EDGE,"E231"),sQuery(id+"F0.wireOp",EDGE,"E232"),sQuery(id+"F0.wireOp",EDGE,"E233"),sQuery(id+"F0.wireOp",EDGE,"E234"),sQuery(id+"F0.wireOp",EDGE,"E235"),sQuery(id+"F0.wireOp",EDGE,"E236"),sQuery(id+"F0.wireOp",EDGE,"E237"),sQuery(id+"F0.wireOp",EDGE,"E238"),sQuery(id+"F0.wireOp",EDGE,"E239"),sQuery(id+"F0.wireOp",EDGE,"E240"),sQuery(id+"F0.wireOp",EDGE,"E241"),sQuery(id+"F0.wireOp",EDGE,"E242"),sQuery(id+"F0.wireOp",EDGE,"E243"),sQuery(id+"F0.wireOp",EDGE,"E244"),sQuery(id+"F0.wireOp",EDGE,"E245"),sQuery(id+"F0.wireOp",EDGE,"E246"),sQuery(id+"F0.wireOp",EDGE,"E247"),sQuery(id+"F0.wireOp",EDGE,"E248"),sQuery(id+"F0.wireOp",EDGE,"E249"),sQuery(id+"F0.wireOp",EDGE,"E250"),sQuery(id+"F0.wireOp",EDGE,"E251"),sQuery(id+"F0.wireOp",EDGE,"E252"),sQuery(id+"F0.wireOp",EDGE,"E253"),sQuery(id+"F0.wireOp",EDGE,"E254"),sQuery(id+"F0.wireOp",EDGE,"E255"),sQuery(id+"F0.wireOp",EDGE,"E256"),sQuery(id+"F0.wireOp",EDGE,"E257"),sQuery(id+"F0.wireOp",EDGE,"E258"),sQuery(id+"F0.wireOp",EDGE,"E259"),sQuery(id+"F0.wireOp",EDGE,"E260"),sQuery(id+"F0.wireOp",EDGE,"E261"),sQuery(id+"F0.wireOp",EDGE,"E265")])]});
            var Q3;
            Q3=makeQuery(id+"F1.opExtrude","SWEPT_BODY",BODY,{"disambiguationData":[OSD([sQuery(id+"F0.wireOp",EDGE,"E143"),sQuery(id+"F0.wireOp",EDGE,"E144"),sQuery(id+"F0.wireOp",EDGE,"E145"),sQuery(id+"F0.wireOp",EDGE,"E146"),sQuery(id+"F0.wireOp",EDGE,"E147"),sQuery(id+"F0.wireOp",EDGE,"E148"),sQuery(id+"F0.wireOp",EDGE,"E149"),sQuery(id+"F0.wireOp",EDGE,"E150"),sQuery(id+"F0.wireOp",EDGE,"E151"),sQuery(id+"F0.wireOp",EDGE,"E152"),sQuery(id+"F0.wireOp",EDGE,"E153"),sQuery(id+"F0.wireOp",EDGE,"E154"),sQuery(id+"F0.wireOp",EDGE,"E155"),sQuery(id+"F0.wireOp",EDGE,"E156"),sQuery(id+"F0.wireOp",EDGE,"E157"),sQuery(id+"F0.wireOp",EDGE,"E158"),sQuery(id+"F0.wireOp",EDGE,"E159"),sQuery(id+"F0.wireOp",EDGE,"E160"),sQuery(id+"F0.wireOp",EDGE,"E161"),sQuery(id+"F0.wireOp",EDGE,"E162"),sQuery(id+"F0.wireOp",EDGE,"E163"),sQuery(id+"F0.wireOp",EDGE,"E164"),sQuery(id+"F0.wireOp",EDGE,"E165"),sQuery(id+"F0.wireOp",EDGE,"E166"),sQuery(id+"F0.wireOp",EDGE,"E167"),sQuery(id+"F0.wireOp",EDGE,"E168"),sQuery(id+"F0.wireOp",EDGE,"E169"),sQuery(id+"F0.wireOp",EDGE,"E170"),sQuery(id+"F0.wireOp",EDGE,"E171"),sQuery(id+"F0.wireOp",EDGE,"E172"),sQuery(id+"F0.wireOp",EDGE,"E173"),sQuery(id+"F0.wireOp",EDGE,"E174"),sQuery(id+"F0.wireOp",EDGE,"E175"),sQuery(id+"F0.wireOp",EDGE,"E176"),sQuery(id+"F0.wireOp",EDGE,"E177"),sQuery(id+"F0.wireOp",EDGE,"E178"),sQuery(id+"F0.wireOp",EDGE,"E179"),sQuery(id+"F0.wireOp",EDGE,"E180"),sQuery(id+"F0.wireOp",EDGE,"E181"),sQuery(id+"F0.wireOp",EDGE,"E182"),sQuery(id+"F0.wireOp",EDGE,"E183"),sQuery(id+"F0.wireOp",EDGE,"E184"),sQuery(id+"F0.wireOp",EDGE,"E185"),sQuery(id+"F0.wireOp",EDGE,"E186"),sQuery(id+"F0.wireOp",EDGE,"E187"),sQuery(id+"F0.wireOp",EDGE,"E188"),sQuery(id+"F0.wireOp",EDGE,"E189"),sQuery(id+"F0.wireOp",EDGE,"E190"),sQuery(id+"F0.wireOp",EDGE,"E191"),sQuery(id+"F0.wireOp",EDGE,"E192"),sQuery(id+"F0.wireOp",EDGE,"E193"),sQuery(id+"F0.wireOp",EDGE,"E194"),sQuery(id+"F0.wireOp",EDGE,"E195"),sQuery(id+"F0.wireOp",EDGE,"E196"),sQuery(id+"F0.wireOp",EDGE,"E197"),sQuery(id+"F0.wireOp",EDGE,"E198"),sQuery(id+"F0.wireOp",EDGE,"E199"),sQuery(id+"F0.wireOp",EDGE,"E200"),sQuery(id+"F0.wireOp",EDGE,"E201"),sQuery(id+"F0.wireOp",EDGE,"E202"),sQuery(id+"F0.wireOp",EDGE,"E203"),sQuery(id+"F0.wireOp",EDGE,"E204"),sQuery(id+"F0.wireOp",EDGE,"E205"),sQuery(id+"F0.wireOp",EDGE,"E262"),sQuery(id+"F0.wireOp",EDGE,"E263")])]});
            var Q4;
            Q4=makeQuery(id+"F1.opExtrude","SWEPT_BODY",BODY,{"disambiguationData":[OSD([sQuery(id+"F0.wireOp",EDGE,"E90"),sQuery(id+"F0.wireOp",EDGE,"E91"),sQuery(id+"F0.wireOp",EDGE,"E92"),sQuery(id+"F0.wireOp",EDGE,"E93"),sQuery(id+"F0.wireOp",EDGE,"E94"),sQuery(id+"F0.wireOp",EDGE,"E95"),sQuery(id+"F0.wireOp",EDGE,"E96"),sQuery(id+"F0.wireOp",EDGE,"E97"),sQuery(id+"F0.wireOp",EDGE,"E98"),sQuery(id+"F0.wireOp",EDGE,"E99"),sQuery(id+"F0.wireOp",EDGE,"E100"),sQuery(id+"F0.wireOp",EDGE,"E101"),sQuery(id+"F0.wireOp",EDGE,"E102"),sQuery(id+"F0.wireOp",EDGE,"E103"),sQuery(id+"F0.wireOp",EDGE,"E104"),sQuery(id+"F0.wireOp",EDGE,"E105"),sQuery(id+"F0.wireOp",EDGE,"E106"),sQuery(id+"F0.wireOp",EDGE,"E107"),sQuery(id+"F0.wireOp",EDGE,"E108"),sQuery(id+"F0.wireOp",EDGE,"E109"),sQuery(id+"F0.wireOp",EDGE,"E110"),sQuery(id+"F0.wireOp",EDGE,"E111"),sQuery(id+"F0.wireOp",EDGE,"E112"),sQuery(id+"F0.wireOp",EDGE,"E113"),sQuery(id+"F0.wireOp",EDGE,"E114"),sQuery(id+"F0.wireOp",EDGE,"E115"),sQuery(id+"F0.wireOp",EDGE,"E116"),sQuery(id+"F0.wireOp",EDGE,"E117"),sQuery(id+"F0.wireOp",EDGE,"E118"),sQuery(id+"F0.wireOp",EDGE,"E119"),sQuery(id+"F0.wireOp",EDGE,"E120"),sQuery(id+"F0.wireOp",EDGE,"E121"),sQuery(id+"F0.wireOp",EDGE,"E122"),sQuery(id+"F0.wireOp",EDGE,"E123"),sQuery(id+"F0.wireOp",EDGE,"E124"),sQuery(id+"F0.wireOp",EDGE,"E125"),sQuery(id+"F0.wireOp",EDGE,"E126"),sQuery(id+"F0.wireOp",EDGE,"E127"),sQuery(id+"F0.wireOp",EDGE,"E128"),sQuery(id+"F0.wireOp",EDGE,"E129"),sQuery(id+"F0.wireOp",EDGE,"E130"),sQuery(id+"F0.wireOp",EDGE,"E131"),sQuery(id+"F0.wireOp",EDGE,"E132"),sQuery(id+"F0.wireOp",EDGE,"E133"),sQuery(id+"F0.wireOp",EDGE,"E134"),sQuery(id+"F0.wireOp",EDGE,"E135"),sQuery(id+"F0.wireOp",EDGE,"E136"),sQuery(id+"F0.wireOp",EDGE,"E137"),sQuery(id+"F0.wireOp",EDGE,"E138"),sQuery(id+"F0.wireOp",EDGE,"E139"),sQuery(id+"F0.wireOp",EDGE,"E140"),sQuery(id+"F0.wireOp",EDGE,"E141"),sQuery(id+"F0.wireOp",EDGE,"E264")])]});
            var Q5;
            Q5=qCreatedBy(makeId("Origin.pointOp"),VERTEX);
            transform(context, id + "F2", {"entities" : qUnion([Q0, Q1, Q2, Q3, Q4]), "transformType" : TransformType.SCALE_UNIFORMLY, "scale" : 0.06, "scalePoint" : qUnion([Q5]), "makeCopy" : false});
        }
    });
